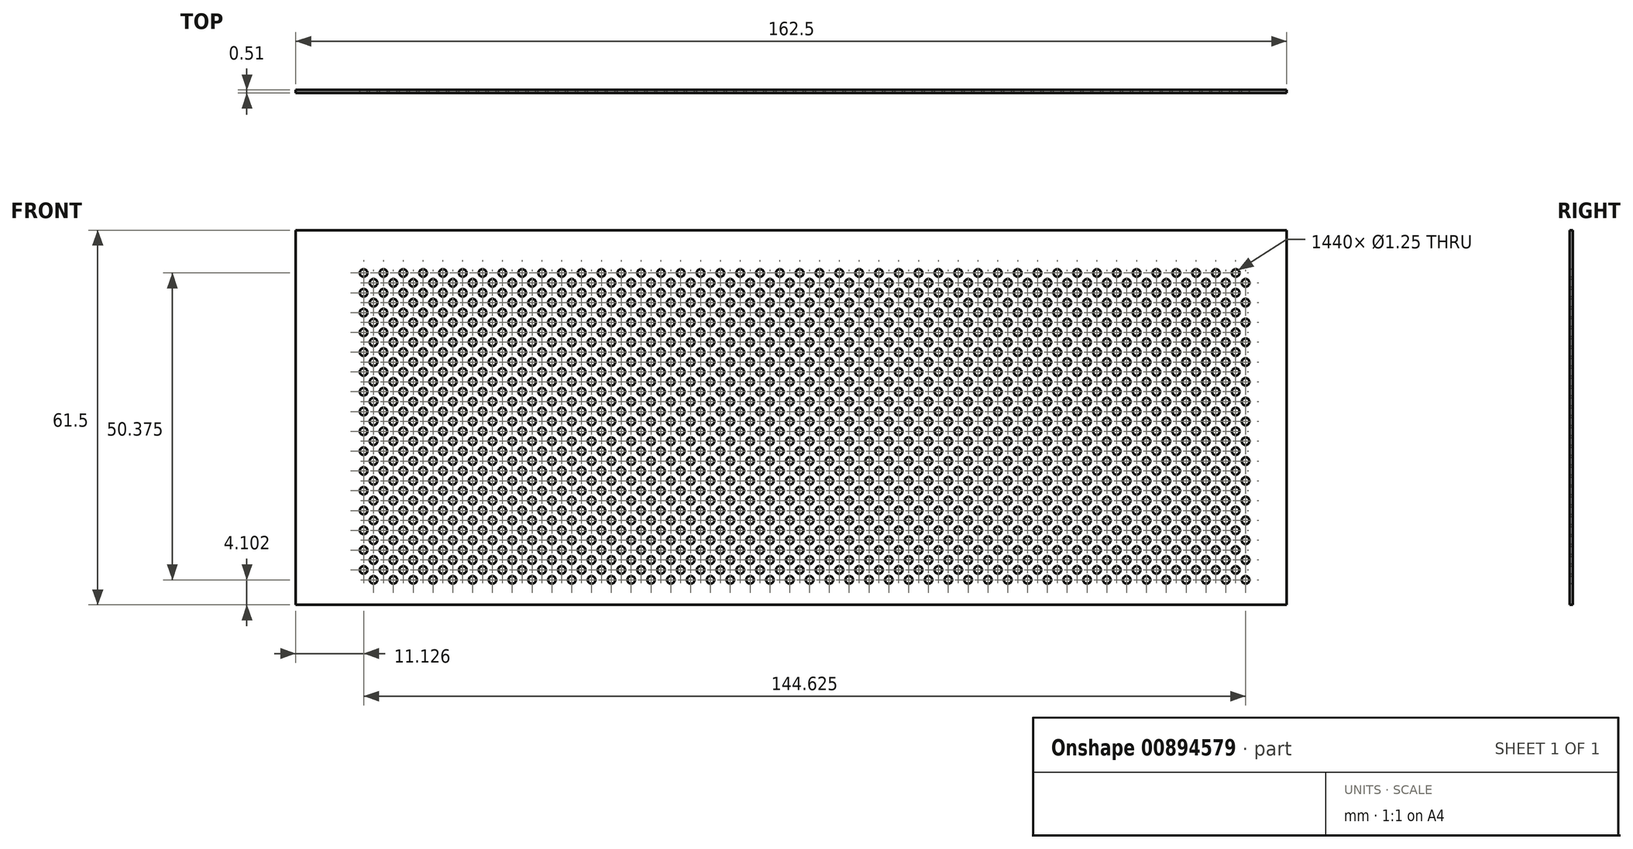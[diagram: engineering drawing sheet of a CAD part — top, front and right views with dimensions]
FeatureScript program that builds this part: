
annotation { "Feature Type Name" : "Feature", "Feature Type Description" : "" }
export const myFeature = defineFeature(function(context is Context, id is Id, definition is map)
    precondition{}
    {
        {
            var Q0;
            Q0=qCreatedBy(makeId("Front.planeOp"),FACE);
            var sketch = newSketch(context, id + "F0", { "sketchPlane" : qUnion([Q0])});
            skLineSegment(sketch, "E0.bottom", {"start": v(-80.2, 17) * mm, "end": v(82.3, 17) * mm});
            skLineSegment(sketch, "E0.top", {"start": v(-80.2, -44.5) * mm, "end": v(82.3, -44.5) * mm});
            skLineSegment(sketch, "E0.left", {"start": v(-80.2, 17) * mm, "end": v(-80.2, -44.5) * mm});
            skLineSegment(sketch, "E0.right", {"start": v(82.3, 17) * mm, "end": v(82.3, -44.5) * mm});
            skCircle(sketch, "E1", {"center": v(-69.07, 9.97) * mm, "radius": 0.62 * mm});
            skCircle(sketch, "E2.0.1.0", {"center": v(-69.07, 6.72) * mm, "radius": 0.62 * mm});
            skCircle(sketch, "E2.0.2.0", {"center": v(-69.07, 3.47) * mm, "radius": 0.62 * mm});
            skCircle(sketch, "E2.1.0.0", {"center": v(-65.82, 9.97) * mm, "radius": 0.62 * mm});
            skCircle(sketch, "E2.1.1.0", {"center": v(-65.82, 6.72) * mm, "radius": 0.62 * mm});
            skCircle(sketch, "E2.1.2.0", {"center": v(-65.82, 3.47) * mm, "radius": 0.62 * mm});
            skCircle(sketch, "E2.2.0.0", {"center": v(-62.57, 9.97) * mm, "radius": 0.62 * mm});
            skCircle(sketch, "E2.2.1.0", {"center": v(-62.57, 6.72) * mm, "radius": 0.62 * mm});
            skCircle(sketch, "E2.2.2.0", {"center": v(-62.57, 3.47) * mm, "radius": 0.62 * mm});
            skCircle(sketch, "E2.3.0.0", {"center": v(-59.32, 9.97) * mm, "radius": 0.62 * mm});
            skCircle(sketch, "E2.3.1.0", {"center": v(-59.32, 6.72) * mm, "radius": 0.62 * mm});
            skCircle(sketch, "E2.3.2.0", {"center": v(-59.32, 3.47) * mm, "radius": 0.62 * mm});
            skCircle(sketch, "E2.4.0.0", {"center": v(-56.07, 9.97) * mm, "radius": 0.62 * mm});
            skCircle(sketch, "E2.4.1.0", {"center": v(-56.07, 6.72) * mm, "radius": 0.62 * mm});
            skCircle(sketch, "E2.4.2.0", {"center": v(-56.07, 3.47) * mm, "radius": 0.62 * mm});
            skCircle(sketch, "E2.5.0.0", {"center": v(-52.82, 9.97) * mm, "radius": 0.62 * mm});
            skCircle(sketch, "E2.5.1.0", {"center": v(-52.82, 6.72) * mm, "radius": 0.62 * mm});
            skCircle(sketch, "E2.5.2.0", {"center": v(-52.82, 3.47) * mm, "radius": 0.62 * mm});
            skCircle(sketch, "E2.6.0.0", {"center": v(-49.57, 9.97) * mm, "radius": 0.62 * mm});
            skCircle(sketch, "E2.6.1.0", {"center": v(-49.57, 6.72) * mm, "radius": 0.62 * mm});
            skCircle(sketch, "E2.6.2.0", {"center": v(-49.57, 3.47) * mm, "radius": 0.62 * mm});
            skCircle(sketch, "E2.7.0.0", {"center": v(-46.32, 9.97) * mm, "radius": 0.62 * mm});
            skCircle(sketch, "E2.7.1.0", {"center": v(-46.32, 6.72) * mm, "radius": 0.62 * mm});
            skCircle(sketch, "E2.7.2.0", {"center": v(-46.32, 3.47) * mm, "radius": 0.62 * mm});
            skCircle(sketch, "E2.8.0.0", {"center": v(-43.07, 9.97) * mm, "radius": 0.62 * mm});
            skCircle(sketch, "E2.8.1.0", {"center": v(-43.07, 6.72) * mm, "radius": 0.62 * mm});
            skCircle(sketch, "E2.8.2.0", {"center": v(-43.07, 3.47) * mm, "radius": 0.62 * mm});
            skCircle(sketch, "E2.9.0.0", {"center": v(-39.82, 9.97) * mm, "radius": 0.62 * mm});
            skCircle(sketch, "E2.9.1.0", {"center": v(-39.82, 6.72) * mm, "radius": 0.62 * mm});
            skCircle(sketch, "E2.9.2.0", {"center": v(-39.82, 3.47) * mm, "radius": 0.62 * mm});
            skCircle(sketch, "E2.10.0.0", {"center": v(-36.57, 9.97) * mm, "radius": 0.62 * mm});
            skCircle(sketch, "E2.10.1.0", {"center": v(-36.57, 6.72) * mm, "radius": 0.62 * mm});
            skCircle(sketch, "E2.10.2.0", {"center": v(-36.57, 3.47) * mm, "radius": 0.62 * mm});
            skCircle(sketch, "E2.11.0.0", {"center": v(-33.32, 9.97) * mm, "radius": 0.62 * mm});
            skCircle(sketch, "E2.11.1.0", {"center": v(-33.32, 6.72) * mm, "radius": 0.62 * mm});
            skCircle(sketch, "E2.11.2.0", {"center": v(-33.32, 3.47) * mm, "radius": 0.62 * mm});
            skCircle(sketch, "E2.12.0.0", {"center": v(-30.07, 9.97) * mm, "radius": 0.62 * mm});
            skCircle(sketch, "E2.12.1.0", {"center": v(-30.07, 6.72) * mm, "radius": 0.62 * mm});
            skCircle(sketch, "E2.12.2.0", {"center": v(-30.07, 3.47) * mm, "radius": 0.62 * mm});
            skCircle(sketch, "E2.13.0.0", {"center": v(-26.82, 9.97) * mm, "radius": 0.62 * mm});
            skCircle(sketch, "E2.13.1.0", {"center": v(-26.82, 6.72) * mm, "radius": 0.62 * mm});
            skCircle(sketch, "E2.13.2.0", {"center": v(-26.82, 3.47) * mm, "radius": 0.62 * mm});
            skCircle(sketch, "E2.14.0.0", {"center": v(-23.57, 9.97) * mm, "radius": 0.62 * mm});
            skCircle(sketch, "E2.14.1.0", {"center": v(-23.57, 6.72) * mm, "radius": 0.62 * mm});
            skCircle(sketch, "E2.14.2.0", {"center": v(-23.57, 3.47) * mm, "radius": 0.62 * mm});
            skCircle(sketch, "E2.15.0.0", {"center": v(-20.32, 9.97) * mm, "radius": 0.62 * mm});
            skCircle(sketch, "E2.15.1.0", {"center": v(-20.32, 6.72) * mm, "radius": 0.62 * mm});
            skCircle(sketch, "E2.15.2.0", {"center": v(-20.32, 3.47) * mm, "radius": 0.62 * mm});
            skCircle(sketch, "E2.16.0.0", {"center": v(-17.07, 9.97) * mm, "radius": 0.62 * mm});
            skCircle(sketch, "E2.16.1.0", {"center": v(-17.07, 6.72) * mm, "radius": 0.62 * mm});
            skCircle(sketch, "E2.16.2.0", {"center": v(-17.07, 3.47) * mm, "radius": 0.62 * mm});
            skCircle(sketch, "E2.17.0.0", {"center": v(-13.82, 9.97) * mm, "radius": 0.62 * mm});
            skCircle(sketch, "E2.17.1.0", {"center": v(-13.82, 6.72) * mm, "radius": 0.62 * mm});
            skCircle(sketch, "E2.17.2.0", {"center": v(-13.82, 3.47) * mm, "radius": 0.62 * mm});
            skCircle(sketch, "E2.18.0.0", {"center": v(-10.57, 9.97) * mm, "radius": 0.62 * mm});
            skCircle(sketch, "E2.18.1.0", {"center": v(-10.57, 6.72) * mm, "radius": 0.62 * mm});
            skCircle(sketch, "E2.18.2.0", {"center": v(-10.57, 3.47) * mm, "radius": 0.62 * mm});
            skCircle(sketch, "E2.19.0.0", {"center": v(-7.32, 9.97) * mm, "radius": 0.62 * mm});
            skCircle(sketch, "E2.19.1.0", {"center": v(-7.32, 6.72) * mm, "radius": 0.62 * mm});
            skCircle(sketch, "E2.19.2.0", {"center": v(-7.32, 3.47) * mm, "radius": 0.62 * mm});
            skLineSegment(sketch, "E2.direction1", {"start": v(-69.07, 9.97) * mm, "end": v(-65.82, 9.97) * mm, "construction": true});
            skLineSegment(sketch, "E2.direction2", {"start": v(-69.07, 9.97) * mm, "end": v(-69.07, 6.72) * mm, "construction": true});
            skCircle(sketch, "E3.0.20.0", {"center": v(-4.07, 9.97) * mm, "radius": 0.62 * mm});
            skCircle(sketch, "E3.0.20.1", {"center": v(-4.07, 6.72) * mm, "radius": 0.62 * mm});
            skCircle(sketch, "E3.0.20.2", {"center": v(-4.07, 3.47) * mm, "radius": 0.62 * mm});
            skCircle(sketch, "E3.0.21.0", {"center": v(-0.82, 9.97) * mm, "radius": 0.62 * mm});
            skCircle(sketch, "E3.0.21.1", {"center": v(-0.82, 6.72) * mm, "radius": 0.62 * mm});
            skCircle(sketch, "E3.0.21.2", {"center": v(-0.82, 3.47) * mm, "radius": 0.62 * mm});
            skCircle(sketch, "E3.0.22.0", {"center": v(2.43, 9.97) * mm, "radius": 0.62 * mm});
            skCircle(sketch, "E3.0.22.1", {"center": v(2.43, 6.72) * mm, "radius": 0.62 * mm});
            skCircle(sketch, "E3.0.22.2", {"center": v(2.43, 3.47) * mm, "radius": 0.62 * mm});
            skCircle(sketch, "E3.0.23.0", {"center": v(5.68, 9.97) * mm, "radius": 0.62 * mm});
            skCircle(sketch, "E3.0.23.1", {"center": v(5.68, 6.72) * mm, "radius": 0.62 * mm});
            skCircle(sketch, "E3.0.23.2", {"center": v(5.68, 3.47) * mm, "radius": 0.62 * mm});
            skCircle(sketch, "E3.0.24.0", {"center": v(8.93, 9.97) * mm, "radius": 0.62 * mm});
            skCircle(sketch, "E3.0.24.1", {"center": v(8.93, 6.72) * mm, "radius": 0.62 * mm});
            skCircle(sketch, "E3.0.24.2", {"center": v(8.93, 3.47) * mm, "radius": 0.62 * mm});
            skCircle(sketch, "E3.0.25.0", {"center": v(12.18, 9.97) * mm, "radius": 0.62 * mm});
            skCircle(sketch, "E3.0.25.1", {"center": v(12.18, 6.72) * mm, "radius": 0.62 * mm});
            skCircle(sketch, "E3.0.25.2", {"center": v(12.18, 3.47) * mm, "radius": 0.62 * mm});
            skCircle(sketch, "E3.0.26.0", {"center": v(15.43, 9.97) * mm, "radius": 0.62 * mm});
            skCircle(sketch, "E3.0.26.1", {"center": v(15.43, 6.72) * mm, "radius": 0.62 * mm});
            skCircle(sketch, "E3.0.26.2", {"center": v(15.43, 3.47) * mm, "radius": 0.62 * mm});
            skCircle(sketch, "E3.0.27.0", {"center": v(18.68, 9.97) * mm, "radius": 0.62 * mm});
            skCircle(sketch, "E3.0.27.1", {"center": v(18.68, 6.72) * mm, "radius": 0.62 * mm});
            skCircle(sketch, "E3.0.27.2", {"center": v(18.68, 3.47) * mm, "radius": 0.62 * mm});
            skCircle(sketch, "E3.0.28.0", {"center": v(21.93, 9.97) * mm, "radius": 0.62 * mm});
            skCircle(sketch, "E3.0.28.1", {"center": v(21.93, 6.72) * mm, "radius": 0.62 * mm});
            skCircle(sketch, "E3.0.28.2", {"center": v(21.93, 3.47) * mm, "radius": 0.62 * mm});
            skCircle(sketch, "E3.0.29.0", {"center": v(25.18, 9.97) * mm, "radius": 0.62 * mm});
            skCircle(sketch, "E3.0.29.1", {"center": v(25.18, 6.72) * mm, "radius": 0.62 * mm});
            skCircle(sketch, "E3.0.29.2", {"center": v(25.18, 3.47) * mm, "radius": 0.62 * mm});
            skCircle(sketch, "E4", {"center": v(-67.45, 8.34) * mm, "radius": 0.62 * mm});
            skLineSegment(sketch, "E5", {"start": v(-65.82, 6.72) * mm, "end": v(-69.07, 9.97) * mm});
            skCircle(sketch, "E6.0.0.3", {"center": v(-69.07, 0.22) * mm, "radius": 0.62 * mm});
            skCircle(sketch, "E6.0.0.4", {"center": v(-69.07, -3.03) * mm, "radius": 0.62 * mm});
            skCircle(sketch, "E6.0.0.5", {"center": v(-69.07, -6.28) * mm, "radius": 0.62 * mm});
            skCircle(sketch, "E6.0.1.3", {"center": v(-65.82, 0.22) * mm, "radius": 0.62 * mm});
            skCircle(sketch, "E6.0.1.4", {"center": v(-65.82, -3.03) * mm, "radius": 0.62 * mm});
            skCircle(sketch, "E6.0.1.5", {"center": v(-65.82, -6.28) * mm, "radius": 0.62 * mm});
            skCircle(sketch, "E6.0.2.3", {"center": v(-62.57, 0.22) * mm, "radius": 0.62 * mm});
            skCircle(sketch, "E6.0.2.4", {"center": v(-62.57, -3.03) * mm, "radius": 0.62 * mm});
            skCircle(sketch, "E6.0.2.5", {"center": v(-62.57, -6.28) * mm, "radius": 0.62 * mm});
            skCircle(sketch, "E6.0.3.3", {"center": v(-59.32, 0.22) * mm, "radius": 0.62 * mm});
            skCircle(sketch, "E6.0.3.4", {"center": v(-59.32, -3.03) * mm, "radius": 0.62 * mm});
            skCircle(sketch, "E6.0.3.5", {"center": v(-59.32, -6.28) * mm, "radius": 0.62 * mm});
            skCircle(sketch, "E6.0.4.3", {"center": v(-56.07, 0.22) * mm, "radius": 0.62 * mm});
            skCircle(sketch, "E6.0.4.4", {"center": v(-56.07, -3.03) * mm, "radius": 0.62 * mm});
            skCircle(sketch, "E6.0.4.5", {"center": v(-56.07, -6.28) * mm, "radius": 0.62 * mm});
            skCircle(sketch, "E6.0.5.3", {"center": v(-52.82, 0.22) * mm, "radius": 0.62 * mm});
            skCircle(sketch, "E6.0.5.4", {"center": v(-52.82, -3.03) * mm, "radius": 0.62 * mm});
            skCircle(sketch, "E6.0.5.5", {"center": v(-52.82, -6.28) * mm, "radius": 0.62 * mm});
            skCircle(sketch, "E6.0.6.3", {"center": v(-49.57, 0.22) * mm, "radius": 0.62 * mm});
            skCircle(sketch, "E6.0.6.4", {"center": v(-49.57, -3.03) * mm, "radius": 0.62 * mm});
            skCircle(sketch, "E6.0.6.5", {"center": v(-49.57, -6.28) * mm, "radius": 0.62 * mm});
            skCircle(sketch, "E6.0.7.3", {"center": v(-46.32, 0.22) * mm, "radius": 0.62 * mm});
            skCircle(sketch, "E6.0.7.4", {"center": v(-46.32, -3.03) * mm, "radius": 0.62 * mm});
            skCircle(sketch, "E6.0.7.5", {"center": v(-46.32, -6.28) * mm, "radius": 0.62 * mm});
            skCircle(sketch, "E6.0.8.3", {"center": v(-43.07, 0.22) * mm, "radius": 0.62 * mm});
            skCircle(sketch, "E6.0.8.4", {"center": v(-43.07, -3.03) * mm, "radius": 0.62 * mm});
            skCircle(sketch, "E6.0.8.5", {"center": v(-43.07, -6.28) * mm, "radius": 0.62 * mm});
            skCircle(sketch, "E6.0.9.3", {"center": v(-39.82, 0.22) * mm, "radius": 0.62 * mm});
            skCircle(sketch, "E6.0.9.4", {"center": v(-39.82, -3.03) * mm, "radius": 0.62 * mm});
            skCircle(sketch, "E6.0.9.5", {"center": v(-39.82, -6.28) * mm, "radius": 0.62 * mm});
            skCircle(sketch, "E6.0.10.3", {"center": v(-36.57, 0.22) * mm, "radius": 0.62 * mm});
            skCircle(sketch, "E6.0.10.4", {"center": v(-36.57, -3.03) * mm, "radius": 0.62 * mm});
            skCircle(sketch, "E6.0.10.5", {"center": v(-36.57, -6.28) * mm, "radius": 0.62 * mm});
            skCircle(sketch, "E6.0.11.3", {"center": v(-33.32, 0.22) * mm, "radius": 0.62 * mm});
            skCircle(sketch, "E6.0.11.4", {"center": v(-33.32, -3.03) * mm, "radius": 0.62 * mm});
            skCircle(sketch, "E6.0.11.5", {"center": v(-33.32, -6.28) * mm, "radius": 0.62 * mm});
            skCircle(sketch, "E6.0.12.3", {"center": v(-30.07, 0.22) * mm, "radius": 0.62 * mm});
            skCircle(sketch, "E6.0.12.4", {"center": v(-30.07, -3.03) * mm, "radius": 0.62 * mm});
            skCircle(sketch, "E6.0.12.5", {"center": v(-30.07, -6.28) * mm, "radius": 0.62 * mm});
            skCircle(sketch, "E6.0.13.3", {"center": v(-26.82, 0.22) * mm, "radius": 0.62 * mm});
            skCircle(sketch, "E6.0.13.4", {"center": v(-26.82, -3.03) * mm, "radius": 0.62 * mm});
            skCircle(sketch, "E6.0.13.5", {"center": v(-26.82, -6.28) * mm, "radius": 0.62 * mm});
            skCircle(sketch, "E6.0.14.3", {"center": v(-23.57, 0.22) * mm, "radius": 0.62 * mm});
            skCircle(sketch, "E6.0.14.4", {"center": v(-23.57, -3.03) * mm, "radius": 0.62 * mm});
            skCircle(sketch, "E6.0.14.5", {"center": v(-23.57, -6.28) * mm, "radius": 0.62 * mm});
            skCircle(sketch, "E6.0.15.3", {"center": v(-20.32, 0.22) * mm, "radius": 0.62 * mm});
            skCircle(sketch, "E6.0.15.4", {"center": v(-20.32, -3.03) * mm, "radius": 0.62 * mm});
            skCircle(sketch, "E6.0.15.5", {"center": v(-20.32, -6.28) * mm, "radius": 0.62 * mm});
            skCircle(sketch, "E6.0.16.3", {"center": v(-17.07, 0.22) * mm, "radius": 0.62 * mm});
            skCircle(sketch, "E6.0.16.4", {"center": v(-17.07, -3.03) * mm, "radius": 0.62 * mm});
            skCircle(sketch, "E6.0.16.5", {"center": v(-17.07, -6.28) * mm, "radius": 0.62 * mm});
            skCircle(sketch, "E6.0.17.3", {"center": v(-13.82, 0.22) * mm, "radius": 0.62 * mm});
            skCircle(sketch, "E6.0.17.4", {"center": v(-13.82, -3.03) * mm, "radius": 0.62 * mm});
            skCircle(sketch, "E6.0.17.5", {"center": v(-13.82, -6.28) * mm, "radius": 0.62 * mm});
            skCircle(sketch, "E6.0.18.3", {"center": v(-10.57, 0.22) * mm, "radius": 0.62 * mm});
            skCircle(sketch, "E6.0.18.4", {"center": v(-10.57, -3.03) * mm, "radius": 0.62 * mm});
            skCircle(sketch, "E6.0.18.5", {"center": v(-10.57, -6.28) * mm, "radius": 0.62 * mm});
            skCircle(sketch, "E6.0.19.3", {"center": v(-7.32, 0.22) * mm, "radius": 0.62 * mm});
            skCircle(sketch, "E6.0.19.4", {"center": v(-7.32, -3.03) * mm, "radius": 0.62 * mm});
            skCircle(sketch, "E6.0.19.5", {"center": v(-7.32, -6.28) * mm, "radius": 0.62 * mm});
            skCircle(sketch, "E6.0.20.3", {"center": v(-4.07, 0.22) * mm, "radius": 0.62 * mm});
            skCircle(sketch, "E6.0.20.4", {"center": v(-4.07, -3.03) * mm, "radius": 0.62 * mm});
            skCircle(sketch, "E6.0.20.5", {"center": v(-4.07, -6.28) * mm, "radius": 0.62 * mm});
            skCircle(sketch, "E6.0.21.3", {"center": v(-0.82, 0.22) * mm, "radius": 0.62 * mm});
            skCircle(sketch, "E6.0.21.4", {"center": v(-0.82, -3.03) * mm, "radius": 0.62 * mm});
            skCircle(sketch, "E6.0.21.5", {"center": v(-0.82, -6.28) * mm, "radius": 0.62 * mm});
            skCircle(sketch, "E6.0.22.3", {"center": v(2.43, 0.22) * mm, "radius": 0.62 * mm});
            skCircle(sketch, "E6.0.22.4", {"center": v(2.43, -3.03) * mm, "radius": 0.62 * mm});
            skCircle(sketch, "E6.0.22.5", {"center": v(2.43, -6.28) * mm, "radius": 0.62 * mm});
            skCircle(sketch, "E6.0.23.3", {"center": v(5.68, 0.22) * mm, "radius": 0.62 * mm});
            skCircle(sketch, "E6.0.23.4", {"center": v(5.68, -3.03) * mm, "radius": 0.62 * mm});
            skCircle(sketch, "E6.0.23.5", {"center": v(5.68, -6.28) * mm, "radius": 0.62 * mm});
            skCircle(sketch, "E6.0.24.3", {"center": v(8.93, 0.22) * mm, "radius": 0.62 * mm});
            skCircle(sketch, "E6.0.24.4", {"center": v(8.93, -3.03) * mm, "radius": 0.62 * mm});
            skCircle(sketch, "E6.0.24.5", {"center": v(8.93, -6.28) * mm, "radius": 0.62 * mm});
            skCircle(sketch, "E6.0.25.3", {"center": v(12.18, 0.22) * mm, "radius": 0.62 * mm});
            skCircle(sketch, "E6.0.25.4", {"center": v(12.18, -3.03) * mm, "radius": 0.62 * mm});
            skCircle(sketch, "E6.0.25.5", {"center": v(12.18, -6.28) * mm, "radius": 0.62 * mm});
            skCircle(sketch, "E6.0.26.3", {"center": v(15.43, 0.22) * mm, "radius": 0.62 * mm});
            skCircle(sketch, "E6.0.26.4", {"center": v(15.43, -3.03) * mm, "radius": 0.62 * mm});
            skCircle(sketch, "E6.0.26.5", {"center": v(15.43, -6.28) * mm, "radius": 0.62 * mm});
            skCircle(sketch, "E6.0.27.3", {"center": v(18.68, 0.22) * mm, "radius": 0.62 * mm});
            skCircle(sketch, "E6.0.27.4", {"center": v(18.68, -3.03) * mm, "radius": 0.62 * mm});
            skCircle(sketch, "E6.0.27.5", {"center": v(18.68, -6.28) * mm, "radius": 0.62 * mm});
            skCircle(sketch, "E6.0.28.3", {"center": v(21.93, 0.22) * mm, "radius": 0.62 * mm});
            skCircle(sketch, "E6.0.28.4", {"center": v(21.93, -3.03) * mm, "radius": 0.62 * mm});
            skCircle(sketch, "E6.0.28.5", {"center": v(21.93, -6.28) * mm, "radius": 0.62 * mm});
            skCircle(sketch, "E6.0.29.3", {"center": v(25.18, 0.22) * mm, "radius": 0.62 * mm});
            skCircle(sketch, "E6.0.29.4", {"center": v(25.18, -3.03) * mm, "radius": 0.62 * mm});
            skCircle(sketch, "E6.0.29.5", {"center": v(25.18, -6.28) * mm, "radius": 0.62 * mm});
            skCircle(sketch, "E7.0.1.0", {"center": v(-67.45, 5.1) * mm, "radius": 0.62 * mm});
            skCircle(sketch, "E7.0.2.0", {"center": v(-67.45, 1.84) * mm, "radius": 0.62 * mm});
            skCircle(sketch, "E7.0.3.0", {"center": v(-67.45, -1.4) * mm, "radius": 0.62 * mm});
            skCircle(sketch, "E7.0.4.0", {"center": v(-67.45, -4.66) * mm, "radius": 0.62 * mm});
            skCircle(sketch, "E7.0.5.0", {"center": v(-67.45, -7.9) * mm, "radius": 0.62 * mm});
            skCircle(sketch, "E7.1.0.0", {"center": v(-64.2, 8.34) * mm, "radius": 0.62 * mm});
            skCircle(sketch, "E7.1.1.0", {"center": v(-64.2, 5.1) * mm, "radius": 0.62 * mm});
            skCircle(sketch, "E7.1.2.0", {"center": v(-64.2, 1.84) * mm, "radius": 0.62 * mm});
            skCircle(sketch, "E7.1.3.0", {"center": v(-64.2, -1.4) * mm, "radius": 0.62 * mm});
            skCircle(sketch, "E7.1.4.0", {"center": v(-64.2, -4.66) * mm, "radius": 0.62 * mm});
            skCircle(sketch, "E7.1.5.0", {"center": v(-64.2, -7.9) * mm, "radius": 0.62 * mm});
            skCircle(sketch, "E7.2.0.0", {"center": v(-60.95, 8.34) * mm, "radius": 0.62 * mm});
            skCircle(sketch, "E7.2.1.0", {"center": v(-60.95, 5.1) * mm, "radius": 0.62 * mm});
            skCircle(sketch, "E7.2.2.0", {"center": v(-60.95, 1.84) * mm, "radius": 0.62 * mm});
            skCircle(sketch, "E7.2.3.0", {"center": v(-60.95, -1.4) * mm, "radius": 0.62 * mm});
            skCircle(sketch, "E7.2.4.0", {"center": v(-60.95, -4.66) * mm, "radius": 0.62 * mm});
            skCircle(sketch, "E7.2.5.0", {"center": v(-60.95, -7.9) * mm, "radius": 0.62 * mm});
            skCircle(sketch, "E7.3.0.0", {"center": v(-57.7, 8.34) * mm, "radius": 0.62 * mm});
            skCircle(sketch, "E7.3.1.0", {"center": v(-57.7, 5.1) * mm, "radius": 0.62 * mm});
            skCircle(sketch, "E7.3.2.0", {"center": v(-57.7, 1.84) * mm, "radius": 0.62 * mm});
            skCircle(sketch, "E7.3.3.0", {"center": v(-57.7, -1.4) * mm, "radius": 0.62 * mm});
            skCircle(sketch, "E7.3.4.0", {"center": v(-57.7, -4.66) * mm, "radius": 0.62 * mm});
            skCircle(sketch, "E7.3.5.0", {"center": v(-57.7, -7.9) * mm, "radius": 0.62 * mm});
            skCircle(sketch, "E7.4.0.0", {"center": v(-54.45, 8.34) * mm, "radius": 0.62 * mm});
            skCircle(sketch, "E7.4.1.0", {"center": v(-54.45, 5.1) * mm, "radius": 0.62 * mm});
            skCircle(sketch, "E7.4.2.0", {"center": v(-54.45, 1.84) * mm, "radius": 0.62 * mm});
            skCircle(sketch, "E7.4.3.0", {"center": v(-54.45, -1.4) * mm, "radius": 0.62 * mm});
            skCircle(sketch, "E7.4.4.0", {"center": v(-54.45, -4.66) * mm, "radius": 0.62 * mm});
            skCircle(sketch, "E7.4.5.0", {"center": v(-54.45, -7.9) * mm, "radius": 0.62 * mm});
            skCircle(sketch, "E7.5.0.0", {"center": v(-51.2, 8.34) * mm, "radius": 0.62 * mm});
            skCircle(sketch, "E7.5.1.0", {"center": v(-51.2, 5.1) * mm, "radius": 0.62 * mm});
            skCircle(sketch, "E7.5.2.0", {"center": v(-51.2, 1.84) * mm, "radius": 0.62 * mm});
            skCircle(sketch, "E7.5.3.0", {"center": v(-51.2, -1.4) * mm, "radius": 0.62 * mm});
            skCircle(sketch, "E7.5.4.0", {"center": v(-51.2, -4.66) * mm, "radius": 0.62 * mm});
            skCircle(sketch, "E7.5.5.0", {"center": v(-51.2, -7.9) * mm, "radius": 0.62 * mm});
            skCircle(sketch, "E7.6.0.0", {"center": v(-47.95, 8.34) * mm, "radius": 0.62 * mm});
            skCircle(sketch, "E7.6.1.0", {"center": v(-47.95, 5.1) * mm, "radius": 0.62 * mm});
            skCircle(sketch, "E7.6.2.0", {"center": v(-47.95, 1.84) * mm, "radius": 0.62 * mm});
            skCircle(sketch, "E7.6.3.0", {"center": v(-47.95, -1.4) * mm, "radius": 0.62 * mm});
            skCircle(sketch, "E7.6.4.0", {"center": v(-47.95, -4.66) * mm, "radius": 0.62 * mm});
            skCircle(sketch, "E7.6.5.0", {"center": v(-47.95, -7.9) * mm, "radius": 0.62 * mm});
            skCircle(sketch, "E7.7.0.0", {"center": v(-44.7, 8.34) * mm, "radius": 0.62 * mm});
            skCircle(sketch, "E7.7.1.0", {"center": v(-44.7, 5.1) * mm, "radius": 0.62 * mm});
            skCircle(sketch, "E7.7.2.0", {"center": v(-44.7, 1.84) * mm, "radius": 0.62 * mm});
            skCircle(sketch, "E7.7.3.0", {"center": v(-44.7, -1.4) * mm, "radius": 0.62 * mm});
            skCircle(sketch, "E7.7.4.0", {"center": v(-44.7, -4.66) * mm, "radius": 0.62 * mm});
            skCircle(sketch, "E7.7.5.0", {"center": v(-44.7, -7.9) * mm, "radius": 0.62 * mm});
            skCircle(sketch, "E7.8.0.0", {"center": v(-41.45, 8.34) * mm, "radius": 0.62 * mm});
            skCircle(sketch, "E7.8.1.0", {"center": v(-41.45, 5.1) * mm, "radius": 0.62 * mm});
            skCircle(sketch, "E7.8.2.0", {"center": v(-41.45, 1.84) * mm, "radius": 0.62 * mm});
            skCircle(sketch, "E7.8.3.0", {"center": v(-41.45, -1.4) * mm, "radius": 0.62 * mm});
            skCircle(sketch, "E7.8.4.0", {"center": v(-41.45, -4.66) * mm, "radius": 0.62 * mm});
            skCircle(sketch, "E7.8.5.0", {"center": v(-41.45, -7.9) * mm, "radius": 0.62 * mm});
            skCircle(sketch, "E7.9.0.0", {"center": v(-38.2, 8.34) * mm, "radius": 0.62 * mm});
            skCircle(sketch, "E7.9.1.0", {"center": v(-38.2, 5.1) * mm, "radius": 0.62 * mm});
            skCircle(sketch, "E7.9.2.0", {"center": v(-38.2, 1.84) * mm, "radius": 0.62 * mm});
            skCircle(sketch, "E7.9.3.0", {"center": v(-38.2, -1.4) * mm, "radius": 0.62 * mm});
            skCircle(sketch, "E7.9.4.0", {"center": v(-38.2, -4.66) * mm, "radius": 0.62 * mm});
            skCircle(sketch, "E7.9.5.0", {"center": v(-38.2, -7.9) * mm, "radius": 0.62 * mm});
            skCircle(sketch, "E7.10.0.0", {"center": v(-34.95, 8.34) * mm, "radius": 0.62 * mm});
            skCircle(sketch, "E7.10.1.0", {"center": v(-34.95, 5.1) * mm, "radius": 0.62 * mm});
            skCircle(sketch, "E7.10.2.0", {"center": v(-34.95, 1.84) * mm, "radius": 0.62 * mm});
            skCircle(sketch, "E7.10.3.0", {"center": v(-34.95, -1.4) * mm, "radius": 0.62 * mm});
            skCircle(sketch, "E7.10.4.0", {"center": v(-34.95, -4.66) * mm, "radius": 0.62 * mm});
            skCircle(sketch, "E7.10.5.0", {"center": v(-34.95, -7.9) * mm, "radius": 0.62 * mm});
            skCircle(sketch, "E7.11.0.0", {"center": v(-31.7, 8.34) * mm, "radius": 0.62 * mm});
            skCircle(sketch, "E7.11.1.0", {"center": v(-31.7, 5.1) * mm, "radius": 0.62 * mm});
            skCircle(sketch, "E7.11.2.0", {"center": v(-31.7, 1.84) * mm, "radius": 0.62 * mm});
            skCircle(sketch, "E7.11.3.0", {"center": v(-31.7, -1.4) * mm, "radius": 0.62 * mm});
            skCircle(sketch, "E7.11.4.0", {"center": v(-31.7, -4.66) * mm, "radius": 0.62 * mm});
            skCircle(sketch, "E7.11.5.0", {"center": v(-31.7, -7.9) * mm, "radius": 0.62 * mm});
            skCircle(sketch, "E7.12.0.0", {"center": v(-28.45, 8.34) * mm, "radius": 0.62 * mm});
            skCircle(sketch, "E7.12.1.0", {"center": v(-28.45, 5.1) * mm, "radius": 0.62 * mm});
            skCircle(sketch, "E7.12.2.0", {"center": v(-28.45, 1.84) * mm, "radius": 0.62 * mm});
            skCircle(sketch, "E7.12.3.0", {"center": v(-28.45, -1.4) * mm, "radius": 0.62 * mm});
            skCircle(sketch, "E7.12.4.0", {"center": v(-28.45, -4.66) * mm, "radius": 0.62 * mm});
            skCircle(sketch, "E7.12.5.0", {"center": v(-28.45, -7.9) * mm, "radius": 0.62 * mm});
            skCircle(sketch, "E7.13.0.0", {"center": v(-25.2, 8.34) * mm, "radius": 0.62 * mm});
            skCircle(sketch, "E7.13.1.0", {"center": v(-25.2, 5.1) * mm, "radius": 0.62 * mm});
            skCircle(sketch, "E7.13.2.0", {"center": v(-25.2, 1.84) * mm, "radius": 0.62 * mm});
            skCircle(sketch, "E7.13.3.0", {"center": v(-25.2, -1.4) * mm, "radius": 0.62 * mm});
            skCircle(sketch, "E7.13.4.0", {"center": v(-25.2, -4.66) * mm, "radius": 0.62 * mm});
            skCircle(sketch, "E7.13.5.0", {"center": v(-25.2, -7.9) * mm, "radius": 0.62 * mm});
            skCircle(sketch, "E7.14.0.0", {"center": v(-21.95, 8.34) * mm, "radius": 0.62 * mm});
            skCircle(sketch, "E7.14.1.0", {"center": v(-21.95, 5.1) * mm, "radius": 0.62 * mm});
            skCircle(sketch, "E7.14.2.0", {"center": v(-21.95, 1.84) * mm, "radius": 0.62 * mm});
            skCircle(sketch, "E7.14.3.0", {"center": v(-21.95, -1.4) * mm, "radius": 0.62 * mm});
            skCircle(sketch, "E7.14.4.0", {"center": v(-21.95, -4.66) * mm, "radius": 0.62 * mm});
            skCircle(sketch, "E7.14.5.0", {"center": v(-21.95, -7.9) * mm, "radius": 0.62 * mm});
            skCircle(sketch, "E7.15.0.0", {"center": v(-18.7, 8.34) * mm, "radius": 0.62 * mm});
            skCircle(sketch, "E7.15.1.0", {"center": v(-18.7, 5.1) * mm, "radius": 0.62 * mm});
            skCircle(sketch, "E7.15.2.0", {"center": v(-18.7, 1.84) * mm, "radius": 0.62 * mm});
            skCircle(sketch, "E7.15.3.0", {"center": v(-18.7, -1.4) * mm, "radius": 0.62 * mm});
            skCircle(sketch, "E7.15.4.0", {"center": v(-18.7, -4.66) * mm, "radius": 0.62 * mm});
            skCircle(sketch, "E7.15.5.0", {"center": v(-18.7, -7.9) * mm, "radius": 0.62 * mm});
            skCircle(sketch, "E7.16.0.0", {"center": v(-15.45, 8.34) * mm, "radius": 0.62 * mm});
            skCircle(sketch, "E7.16.1.0", {"center": v(-15.45, 5.1) * mm, "radius": 0.62 * mm});
            skCircle(sketch, "E7.16.2.0", {"center": v(-15.45, 1.84) * mm, "radius": 0.62 * mm});
            skCircle(sketch, "E7.16.3.0", {"center": v(-15.45, -1.4) * mm, "radius": 0.62 * mm});
            skCircle(sketch, "E7.16.4.0", {"center": v(-15.45, -4.66) * mm, "radius": 0.62 * mm});
            skCircle(sketch, "E7.16.5.0", {"center": v(-15.45, -7.9) * mm, "radius": 0.62 * mm});
            skCircle(sketch, "E7.17.0.0", {"center": v(-12.2, 8.34) * mm, "radius": 0.62 * mm});
            skCircle(sketch, "E7.17.1.0", {"center": v(-12.2, 5.1) * mm, "radius": 0.62 * mm});
            skCircle(sketch, "E7.17.2.0", {"center": v(-12.2, 1.84) * mm, "radius": 0.62 * mm});
            skCircle(sketch, "E7.17.3.0", {"center": v(-12.2, -1.4) * mm, "radius": 0.62 * mm});
            skCircle(sketch, "E7.17.4.0", {"center": v(-12.2, -4.66) * mm, "radius": 0.62 * mm});
            skCircle(sketch, "E7.17.5.0", {"center": v(-12.2, -7.9) * mm, "radius": 0.62 * mm});
            skCircle(sketch, "E7.18.0.0", {"center": v(-8.95, 8.34) * mm, "radius": 0.62 * mm});
            skCircle(sketch, "E7.18.1.0", {"center": v(-8.95, 5.1) * mm, "radius": 0.62 * mm});
            skCircle(sketch, "E7.18.2.0", {"center": v(-8.95, 1.84) * mm, "radius": 0.62 * mm});
            skCircle(sketch, "E7.18.3.0", {"center": v(-8.95, -1.4) * mm, "radius": 0.62 * mm});
            skCircle(sketch, "E7.18.4.0", {"center": v(-8.95, -4.66) * mm, "radius": 0.62 * mm});
            skCircle(sketch, "E7.18.5.0", {"center": v(-8.95, -7.9) * mm, "radius": 0.62 * mm});
            skCircle(sketch, "E7.19.0.0", {"center": v(-5.7, 8.34) * mm, "radius": 0.62 * mm});
            skCircle(sketch, "E7.19.1.0", {"center": v(-5.7, 5.1) * mm, "radius": 0.62 * mm});
            skCircle(sketch, "E7.19.2.0", {"center": v(-5.7, 1.84) * mm, "radius": 0.62 * mm});
            skCircle(sketch, "E7.19.3.0", {"center": v(-5.7, -1.4) * mm, "radius": 0.62 * mm});
            skCircle(sketch, "E7.19.4.0", {"center": v(-5.7, -4.66) * mm, "radius": 0.62 * mm});
            skCircle(sketch, "E7.19.5.0", {"center": v(-5.7, -7.9) * mm, "radius": 0.62 * mm});
            skCircle(sketch, "E7.20.0.0", {"center": v(-2.45, 8.34) * mm, "radius": 0.62 * mm});
            skCircle(sketch, "E7.20.1.0", {"center": v(-2.45, 5.1) * mm, "radius": 0.62 * mm});
            skCircle(sketch, "E7.20.2.0", {"center": v(-2.45, 1.84) * mm, "radius": 0.62 * mm});
            skCircle(sketch, "E7.20.3.0", {"center": v(-2.45, -1.4) * mm, "radius": 0.62 * mm});
            skCircle(sketch, "E7.20.4.0", {"center": v(-2.45, -4.66) * mm, "radius": 0.62 * mm});
            skCircle(sketch, "E7.20.5.0", {"center": v(-2.45, -7.9) * mm, "radius": 0.62 * mm});
            skCircle(sketch, "E7.21.0.0", {"center": v(0.8, 8.34) * mm, "radius": 0.62 * mm});
            skCircle(sketch, "E7.21.1.0", {"center": v(0.8, 5.1) * mm, "radius": 0.62 * mm});
            skCircle(sketch, "E7.21.2.0", {"center": v(0.8, 1.84) * mm, "radius": 0.62 * mm});
            skCircle(sketch, "E7.21.3.0", {"center": v(0.8, -1.4) * mm, "radius": 0.62 * mm});
            skCircle(sketch, "E7.21.4.0", {"center": v(0.8, -4.66) * mm, "radius": 0.62 * mm});
            skCircle(sketch, "E7.21.5.0", {"center": v(0.8, -7.9) * mm, "radius": 0.62 * mm});
            skCircle(sketch, "E7.22.0.0", {"center": v(4.05, 8.34) * mm, "radius": 0.62 * mm});
            skCircle(sketch, "E7.22.1.0", {"center": v(4.05, 5.1) * mm, "radius": 0.62 * mm});
            skCircle(sketch, "E7.22.2.0", {"center": v(4.05, 1.84) * mm, "radius": 0.62 * mm});
            skCircle(sketch, "E7.22.3.0", {"center": v(4.05, -1.4) * mm, "radius": 0.62 * mm});
            skCircle(sketch, "E7.22.4.0", {"center": v(4.05, -4.66) * mm, "radius": 0.62 * mm});
            skCircle(sketch, "E7.22.5.0", {"center": v(4.05, -7.9) * mm, "radius": 0.62 * mm});
            skCircle(sketch, "E7.23.0.0", {"center": v(7.3, 8.34) * mm, "radius": 0.62 * mm});
            skCircle(sketch, "E7.23.1.0", {"center": v(7.3, 5.1) * mm, "radius": 0.62 * mm});
            skCircle(sketch, "E7.23.2.0", {"center": v(7.3, 1.84) * mm, "radius": 0.62 * mm});
            skCircle(sketch, "E7.23.3.0", {"center": v(7.3, -1.4) * mm, "radius": 0.62 * mm});
            skCircle(sketch, "E7.23.4.0", {"center": v(7.3, -4.66) * mm, "radius": 0.62 * mm});
            skCircle(sketch, "E7.23.5.0", {"center": v(7.3, -7.9) * mm, "radius": 0.62 * mm});
            skCircle(sketch, "E7.24.0.0", {"center": v(10.55, 8.34) * mm, "radius": 0.62 * mm});
            skCircle(sketch, "E7.24.1.0", {"center": v(10.55, 5.1) * mm, "radius": 0.62 * mm});
            skCircle(sketch, "E7.24.2.0", {"center": v(10.55, 1.84) * mm, "radius": 0.62 * mm});
            skCircle(sketch, "E7.24.3.0", {"center": v(10.55, -1.4) * mm, "radius": 0.62 * mm});
            skCircle(sketch, "E7.24.4.0", {"center": v(10.55, -4.66) * mm, "radius": 0.62 * mm});
            skCircle(sketch, "E7.24.5.0", {"center": v(10.55, -7.9) * mm, "radius": 0.62 * mm});
            skCircle(sketch, "E7.25.0.0", {"center": v(13.8, 8.34) * mm, "radius": 0.62 * mm});
            skCircle(sketch, "E7.25.1.0", {"center": v(13.8, 5.1) * mm, "radius": 0.62 * mm});
            skCircle(sketch, "E7.25.2.0", {"center": v(13.8, 1.84) * mm, "radius": 0.62 * mm});
            skCircle(sketch, "E7.25.3.0", {"center": v(13.8, -1.4) * mm, "radius": 0.62 * mm});
            skCircle(sketch, "E7.25.4.0", {"center": v(13.8, -4.66) * mm, "radius": 0.62 * mm});
            skCircle(sketch, "E7.25.5.0", {"center": v(13.8, -7.9) * mm, "radius": 0.62 * mm});
            skCircle(sketch, "E7.26.0.0", {"center": v(17.05, 8.34) * mm, "radius": 0.62 * mm});
            skCircle(sketch, "E7.26.1.0", {"center": v(17.05, 5.1) * mm, "radius": 0.62 * mm});
            skCircle(sketch, "E7.26.2.0", {"center": v(17.05, 1.84) * mm, "radius": 0.62 * mm});
            skCircle(sketch, "E7.26.3.0", {"center": v(17.05, -1.4) * mm, "radius": 0.62 * mm});
            skCircle(sketch, "E7.26.4.0", {"center": v(17.05, -4.66) * mm, "radius": 0.62 * mm});
            skCircle(sketch, "E7.26.5.0", {"center": v(17.05, -7.9) * mm, "radius": 0.62 * mm});
            skCircle(sketch, "E7.27.0.0", {"center": v(20.3, 8.34) * mm, "radius": 0.62 * mm});
            skCircle(sketch, "E7.27.1.0", {"center": v(20.3, 5.1) * mm, "radius": 0.62 * mm});
            skCircle(sketch, "E7.27.2.0", {"center": v(20.3, 1.84) * mm, "radius": 0.62 * mm});
            skCircle(sketch, "E7.27.3.0", {"center": v(20.3, -1.4) * mm, "radius": 0.62 * mm});
            skCircle(sketch, "E7.27.4.0", {"center": v(20.3, -4.66) * mm, "radius": 0.62 * mm});
            skCircle(sketch, "E7.27.5.0", {"center": v(20.3, -7.9) * mm, "radius": 0.62 * mm});
            skCircle(sketch, "E7.28.0.0", {"center": v(23.55, 8.34) * mm, "radius": 0.62 * mm});
            skCircle(sketch, "E7.28.1.0", {"center": v(23.55, 5.1) * mm, "radius": 0.62 * mm});
            skCircle(sketch, "E7.28.2.0", {"center": v(23.55, 1.84) * mm, "radius": 0.62 * mm});
            skCircle(sketch, "E7.28.3.0", {"center": v(23.55, -1.4) * mm, "radius": 0.62 * mm});
            skCircle(sketch, "E7.28.4.0", {"center": v(23.55, -4.66) * mm, "radius": 0.62 * mm});
            skCircle(sketch, "E7.28.5.0", {"center": v(23.55, -7.9) * mm, "radius": 0.62 * mm});
            skCircle(sketch, "E7.29.0.0", {"center": v(26.8, 8.34) * mm, "radius": 0.62 * mm});
            skCircle(sketch, "E7.29.1.0", {"center": v(26.8, 5.1) * mm, "radius": 0.62 * mm});
            skCircle(sketch, "E7.29.2.0", {"center": v(26.8, 1.84) * mm, "radius": 0.62 * mm});
            skCircle(sketch, "E7.29.3.0", {"center": v(26.8, -1.4) * mm, "radius": 0.62 * mm});
            skCircle(sketch, "E7.29.4.0", {"center": v(26.8, -4.66) * mm, "radius": 0.62 * mm});
            skCircle(sketch, "E7.29.5.0", {"center": v(26.8, -7.9) * mm, "radius": 0.62 * mm});
            skLineSegment(sketch, "E7.direction1", {"start": v(-67.45, 8.34) * mm, "end": v(-64.2, 8.34) * mm, "construction": true});
            skLineSegment(sketch, "E7.direction2", {"start": v(-67.45, 8.34) * mm, "end": v(-67.45, 5.1) * mm, "construction": true});
            skCircle(sketch, "E8.0.30.0", {"center": v(28.43, 9.97) * mm, "radius": 0.62 * mm});
            skCircle(sketch, "E8.0.30.1", {"center": v(28.43, 6.72) * mm, "radius": 0.62 * mm});
            skCircle(sketch, "E8.0.30.2", {"center": v(28.43, 3.47) * mm, "radius": 0.62 * mm});
            skCircle(sketch, "E8.0.30.3", {"center": v(28.43, 0.22) * mm, "radius": 0.62 * mm});
            skCircle(sketch, "E8.0.30.4", {"center": v(28.43, -3.03) * mm, "radius": 0.62 * mm});
            skCircle(sketch, "E8.0.30.5", {"center": v(28.43, -6.28) * mm, "radius": 0.62 * mm});
            skCircle(sketch, "E8.0.31.0", {"center": v(31.68, 9.97) * mm, "radius": 0.62 * mm});
            skCircle(sketch, "E8.0.31.1", {"center": v(31.68, 6.72) * mm, "radius": 0.62 * mm});
            skCircle(sketch, "E8.0.31.2", {"center": v(31.68, 3.47) * mm, "radius": 0.62 * mm});
            skCircle(sketch, "E8.0.31.3", {"center": v(31.68, 0.22) * mm, "radius": 0.62 * mm});
            skCircle(sketch, "E8.0.31.4", {"center": v(31.68, -3.03) * mm, "radius": 0.62 * mm});
            skCircle(sketch, "E8.0.31.5", {"center": v(31.68, -6.28) * mm, "radius": 0.62 * mm});
            skCircle(sketch, "E8.0.32.0", {"center": v(34.93, 9.97) * mm, "radius": 0.62 * mm});
            skCircle(sketch, "E8.0.32.1", {"center": v(34.93, 6.72) * mm, "radius": 0.62 * mm});
            skCircle(sketch, "E8.0.32.2", {"center": v(34.93, 3.47) * mm, "radius": 0.62 * mm});
            skCircle(sketch, "E8.0.32.3", {"center": v(34.93, 0.22) * mm, "radius": 0.62 * mm});
            skCircle(sketch, "E8.0.32.4", {"center": v(34.93, -3.03) * mm, "radius": 0.62 * mm});
            skCircle(sketch, "E8.0.32.5", {"center": v(34.93, -6.28) * mm, "radius": 0.62 * mm});
            skCircle(sketch, "E8.0.33.0", {"center": v(38.18, 9.97) * mm, "radius": 0.62 * mm});
            skCircle(sketch, "E8.0.33.1", {"center": v(38.18, 6.72) * mm, "radius": 0.62 * mm});
            skCircle(sketch, "E8.0.33.2", {"center": v(38.18, 3.47) * mm, "radius": 0.62 * mm});
            skCircle(sketch, "E8.0.33.3", {"center": v(38.18, 0.22) * mm, "radius": 0.62 * mm});
            skCircle(sketch, "E8.0.33.4", {"center": v(38.18, -3.03) * mm, "radius": 0.62 * mm});
            skCircle(sketch, "E8.0.33.5", {"center": v(38.18, -6.28) * mm, "radius": 0.62 * mm});
            skCircle(sketch, "E8.0.34.0", {"center": v(41.43, 9.97) * mm, "radius": 0.62 * mm});
            skCircle(sketch, "E8.0.34.1", {"center": v(41.43, 6.72) * mm, "radius": 0.62 * mm});
            skCircle(sketch, "E8.0.34.2", {"center": v(41.43, 3.47) * mm, "radius": 0.62 * mm});
            skCircle(sketch, "E8.0.34.3", {"center": v(41.43, 0.22) * mm, "radius": 0.62 * mm});
            skCircle(sketch, "E8.0.34.4", {"center": v(41.43, -3.03) * mm, "radius": 0.62 * mm});
            skCircle(sketch, "E8.0.34.5", {"center": v(41.43, -6.28) * mm, "radius": 0.62 * mm});
            skCircle(sketch, "E8.0.35.0", {"center": v(44.68, 9.97) * mm, "radius": 0.62 * mm});
            skCircle(sketch, "E8.0.35.1", {"center": v(44.68, 6.72) * mm, "radius": 0.62 * mm});
            skCircle(sketch, "E8.0.35.2", {"center": v(44.68, 3.47) * mm, "radius": 0.62 * mm});
            skCircle(sketch, "E8.0.35.3", {"center": v(44.68, 0.22) * mm, "radius": 0.62 * mm});
            skCircle(sketch, "E8.0.35.4", {"center": v(44.68, -3.03) * mm, "radius": 0.62 * mm});
            skCircle(sketch, "E8.0.35.5", {"center": v(44.68, -6.28) * mm, "radius": 0.62 * mm});
            skCircle(sketch, "E8.0.36.0", {"center": v(47.93, 9.97) * mm, "radius": 0.62 * mm});
            skCircle(sketch, "E8.0.36.1", {"center": v(47.93, 6.72) * mm, "radius": 0.62 * mm});
            skCircle(sketch, "E8.0.36.2", {"center": v(47.93, 3.47) * mm, "radius": 0.62 * mm});
            skCircle(sketch, "E8.0.36.3", {"center": v(47.93, 0.22) * mm, "radius": 0.62 * mm});
            skCircle(sketch, "E8.0.36.4", {"center": v(47.93, -3.03) * mm, "radius": 0.62 * mm});
            skCircle(sketch, "E8.0.36.5", {"center": v(47.93, -6.28) * mm, "radius": 0.62 * mm});
            skCircle(sketch, "E8.0.37.0", {"center": v(51.18, 9.97) * mm, "radius": 0.62 * mm});
            skCircle(sketch, "E8.0.37.1", {"center": v(51.18, 6.72) * mm, "radius": 0.62 * mm});
            skCircle(sketch, "E8.0.37.2", {"center": v(51.18, 3.47) * mm, "radius": 0.62 * mm});
            skCircle(sketch, "E8.0.37.3", {"center": v(51.18, 0.22) * mm, "radius": 0.62 * mm});
            skCircle(sketch, "E8.0.37.4", {"center": v(51.18, -3.03) * mm, "radius": 0.62 * mm});
            skCircle(sketch, "E8.0.37.5", {"center": v(51.18, -6.28) * mm, "radius": 0.62 * mm});
            skCircle(sketch, "E8.0.38.0", {"center": v(54.43, 9.97) * mm, "radius": 0.62 * mm});
            skCircle(sketch, "E8.0.38.1", {"center": v(54.43, 6.72) * mm, "radius": 0.62 * mm});
            skCircle(sketch, "E8.0.38.2", {"center": v(54.43, 3.47) * mm, "radius": 0.62 * mm});
            skCircle(sketch, "E8.0.38.3", {"center": v(54.43, 0.22) * mm, "radius": 0.62 * mm});
            skCircle(sketch, "E8.0.38.4", {"center": v(54.43, -3.03) * mm, "radius": 0.62 * mm});
            skCircle(sketch, "E8.0.38.5", {"center": v(54.43, -6.28) * mm, "radius": 0.62 * mm});
            skCircle(sketch, "E8.0.39.0", {"center": v(57.68, 9.97) * mm, "radius": 0.62 * mm});
            skCircle(sketch, "E8.0.39.1", {"center": v(57.68, 6.72) * mm, "radius": 0.62 * mm});
            skCircle(sketch, "E8.0.39.2", {"center": v(57.68, 3.47) * mm, "radius": 0.62 * mm});
            skCircle(sketch, "E8.0.39.3", {"center": v(57.68, 0.22) * mm, "radius": 0.62 * mm});
            skCircle(sketch, "E8.0.39.4", {"center": v(57.68, -3.03) * mm, "radius": 0.62 * mm});
            skCircle(sketch, "E8.0.39.5", {"center": v(57.68, -6.28) * mm, "radius": 0.62 * mm});
            skCircle(sketch, "E8.0.40.0", {"center": v(60.93, 9.97) * mm, "radius": 0.62 * mm});
            skCircle(sketch, "E8.0.40.1", {"center": v(60.93, 6.72) * mm, "radius": 0.62 * mm});
            skCircle(sketch, "E8.0.40.2", {"center": v(60.93, 3.47) * mm, "radius": 0.62 * mm});
            skCircle(sketch, "E8.0.40.3", {"center": v(60.93, 0.22) * mm, "radius": 0.62 * mm});
            skCircle(sketch, "E8.0.40.4", {"center": v(60.93, -3.03) * mm, "radius": 0.62 * mm});
            skCircle(sketch, "E8.0.40.5", {"center": v(60.93, -6.28) * mm, "radius": 0.62 * mm});
            skCircle(sketch, "E8.0.41.0", {"center": v(64.18, 9.97) * mm, "radius": 0.62 * mm});
            skCircle(sketch, "E8.0.41.1", {"center": v(64.18, 6.72) * mm, "radius": 0.62 * mm});
            skCircle(sketch, "E8.0.41.2", {"center": v(64.18, 3.47) * mm, "radius": 0.62 * mm});
            skCircle(sketch, "E8.0.41.3", {"center": v(64.18, 0.22) * mm, "radius": 0.62 * mm});
            skCircle(sketch, "E8.0.41.4", {"center": v(64.18, -3.03) * mm, "radius": 0.62 * mm});
            skCircle(sketch, "E8.0.41.5", {"center": v(64.18, -6.28) * mm, "radius": 0.62 * mm});
            skCircle(sketch, "E8.0.42.0", {"center": v(67.43, 9.97) * mm, "radius": 0.62 * mm});
            skCircle(sketch, "E8.0.42.1", {"center": v(67.43, 6.72) * mm, "radius": 0.62 * mm});
            skCircle(sketch, "E8.0.42.2", {"center": v(67.43, 3.47) * mm, "radius": 0.62 * mm});
            skCircle(sketch, "E8.0.42.3", {"center": v(67.43, 0.22) * mm, "radius": 0.62 * mm});
            skCircle(sketch, "E8.0.42.4", {"center": v(67.43, -3.03) * mm, "radius": 0.62 * mm});
            skCircle(sketch, "E8.0.42.5", {"center": v(67.43, -6.28) * mm, "radius": 0.62 * mm});
            skCircle(sketch, "E8.0.43.0", {"center": v(70.68, 9.97) * mm, "radius": 0.62 * mm});
            skCircle(sketch, "E8.0.43.1", {"center": v(70.68, 6.72) * mm, "radius": 0.62 * mm});
            skCircle(sketch, "E8.0.43.2", {"center": v(70.68, 3.47) * mm, "radius": 0.62 * mm});
            skCircle(sketch, "E8.0.43.3", {"center": v(70.68, 0.22) * mm, "radius": 0.62 * mm});
            skCircle(sketch, "E8.0.43.4", {"center": v(70.68, -3.03) * mm, "radius": 0.62 * mm});
            skCircle(sketch, "E8.0.43.5", {"center": v(70.68, -6.28) * mm, "radius": 0.62 * mm});
            skCircle(sketch, "E8.0.44.0", {"center": v(73.93, 9.97) * mm, "radius": 0.62 * mm});
            skCircle(sketch, "E8.0.44.1", {"center": v(73.93, 6.72) * mm, "radius": 0.62 * mm});
            skCircle(sketch, "E8.0.44.2", {"center": v(73.93, 3.47) * mm, "radius": 0.62 * mm});
            skCircle(sketch, "E8.0.44.3", {"center": v(73.93, 0.22) * mm, "radius": 0.62 * mm});
            skCircle(sketch, "E8.0.44.4", {"center": v(73.93, -3.03) * mm, "radius": 0.62 * mm});
            skCircle(sketch, "E8.0.44.5", {"center": v(73.93, -6.28) * mm, "radius": 0.62 * mm});
            skCircle(sketch, "E9.0.30.0", {"center": v(30.05, 8.34) * mm, "radius": 0.62 * mm});
            skCircle(sketch, "E9.0.30.1", {"center": v(30.05, 5.1) * mm, "radius": 0.62 * mm});
            skCircle(sketch, "E9.0.30.2", {"center": v(30.05, 1.84) * mm, "radius": 0.62 * mm});
            skCircle(sketch, "E9.0.30.3", {"center": v(30.05, -1.4) * mm, "radius": 0.62 * mm});
            skCircle(sketch, "E9.0.30.4", {"center": v(30.05, -4.66) * mm, "radius": 0.62 * mm});
            skCircle(sketch, "E9.0.30.5", {"center": v(30.05, -7.9) * mm, "radius": 0.62 * mm});
            skCircle(sketch, "E9.0.31.0", {"center": v(33.3, 8.34) * mm, "radius": 0.62 * mm});
            skCircle(sketch, "E9.0.31.1", {"center": v(33.3, 5.1) * mm, "radius": 0.62 * mm});
            skCircle(sketch, "E9.0.31.2", {"center": v(33.3, 1.84) * mm, "radius": 0.62 * mm});
            skCircle(sketch, "E9.0.31.3", {"center": v(33.3, -1.4) * mm, "radius": 0.62 * mm});
            skCircle(sketch, "E9.0.31.4", {"center": v(33.3, -4.66) * mm, "radius": 0.62 * mm});
            skCircle(sketch, "E9.0.31.5", {"center": v(33.3, -7.9) * mm, "radius": 0.62 * mm});
            skCircle(sketch, "E9.0.32.0", {"center": v(36.55, 8.34) * mm, "radius": 0.62 * mm});
            skCircle(sketch, "E9.0.32.1", {"center": v(36.55, 5.1) * mm, "radius": 0.62 * mm});
            skCircle(sketch, "E9.0.32.2", {"center": v(36.55, 1.84) * mm, "radius": 0.62 * mm});
            skCircle(sketch, "E9.0.32.3", {"center": v(36.55, -1.4) * mm, "radius": 0.62 * mm});
            skCircle(sketch, "E9.0.32.4", {"center": v(36.55, -4.66) * mm, "radius": 0.62 * mm});
            skCircle(sketch, "E9.0.32.5", {"center": v(36.55, -7.9) * mm, "radius": 0.62 * mm});
            skCircle(sketch, "E9.0.33.0", {"center": v(39.8, 8.34) * mm, "radius": 0.62 * mm});
            skCircle(sketch, "E9.0.33.1", {"center": v(39.8, 5.1) * mm, "radius": 0.62 * mm});
            skCircle(sketch, "E9.0.33.2", {"center": v(39.8, 1.84) * mm, "radius": 0.62 * mm});
            skCircle(sketch, "E9.0.33.3", {"center": v(39.8, -1.4) * mm, "radius": 0.62 * mm});
            skCircle(sketch, "E9.0.33.4", {"center": v(39.8, -4.66) * mm, "radius": 0.62 * mm});
            skCircle(sketch, "E9.0.33.5", {"center": v(39.8, -7.9) * mm, "radius": 0.62 * mm});
            skCircle(sketch, "E9.0.34.0", {"center": v(43.05, 8.34) * mm, "radius": 0.62 * mm});
            skCircle(sketch, "E9.0.34.1", {"center": v(43.05, 5.1) * mm, "radius": 0.62 * mm});
            skCircle(sketch, "E9.0.34.2", {"center": v(43.05, 1.84) * mm, "radius": 0.62 * mm});
            skCircle(sketch, "E9.0.34.3", {"center": v(43.05, -1.4) * mm, "radius": 0.62 * mm});
            skCircle(sketch, "E9.0.34.4", {"center": v(43.05, -4.66) * mm, "radius": 0.62 * mm});
            skCircle(sketch, "E9.0.34.5", {"center": v(43.05, -7.9) * mm, "radius": 0.62 * mm});
            skCircle(sketch, "E9.0.35.0", {"center": v(46.3, 8.34) * mm, "radius": 0.62 * mm});
            skCircle(sketch, "E9.0.35.1", {"center": v(46.3, 5.1) * mm, "radius": 0.62 * mm});
            skCircle(sketch, "E9.0.35.2", {"center": v(46.3, 1.84) * mm, "radius": 0.62 * mm});
            skCircle(sketch, "E9.0.35.3", {"center": v(46.3, -1.4) * mm, "radius": 0.62 * mm});
            skCircle(sketch, "E9.0.35.4", {"center": v(46.3, -4.66) * mm, "radius": 0.62 * mm});
            skCircle(sketch, "E9.0.35.5", {"center": v(46.3, -7.9) * mm, "radius": 0.62 * mm});
            skCircle(sketch, "E9.0.36.0", {"center": v(49.55, 8.34) * mm, "radius": 0.62 * mm});
            skCircle(sketch, "E9.0.36.1", {"center": v(49.55, 5.1) * mm, "radius": 0.62 * mm});
            skCircle(sketch, "E9.0.36.2", {"center": v(49.55, 1.84) * mm, "radius": 0.62 * mm});
            skCircle(sketch, "E9.0.36.3", {"center": v(49.55, -1.4) * mm, "radius": 0.62 * mm});
            skCircle(sketch, "E9.0.36.4", {"center": v(49.55, -4.66) * mm, "radius": 0.62 * mm});
            skCircle(sketch, "E9.0.36.5", {"center": v(49.55, -7.9) * mm, "radius": 0.62 * mm});
            skCircle(sketch, "E9.0.37.0", {"center": v(52.8, 8.34) * mm, "radius": 0.62 * mm});
            skCircle(sketch, "E9.0.37.1", {"center": v(52.8, 5.1) * mm, "radius": 0.62 * mm});
            skCircle(sketch, "E9.0.37.2", {"center": v(52.8, 1.84) * mm, "radius": 0.62 * mm});
            skCircle(sketch, "E9.0.37.3", {"center": v(52.8, -1.4) * mm, "radius": 0.62 * mm});
            skCircle(sketch, "E9.0.37.4", {"center": v(52.8, -4.66) * mm, "radius": 0.62 * mm});
            skCircle(sketch, "E9.0.37.5", {"center": v(52.8, -7.9) * mm, "radius": 0.62 * mm});
            skCircle(sketch, "E9.0.38.0", {"center": v(56.05, 8.34) * mm, "radius": 0.62 * mm});
            skCircle(sketch, "E9.0.38.1", {"center": v(56.05, 5.1) * mm, "radius": 0.62 * mm});
            skCircle(sketch, "E9.0.38.2", {"center": v(56.05, 1.84) * mm, "radius": 0.62 * mm});
            skCircle(sketch, "E9.0.38.3", {"center": v(56.05, -1.4) * mm, "radius": 0.62 * mm});
            skCircle(sketch, "E9.0.38.4", {"center": v(56.05, -4.66) * mm, "radius": 0.62 * mm});
            skCircle(sketch, "E9.0.38.5", {"center": v(56.05, -7.9) * mm, "radius": 0.62 * mm});
            skCircle(sketch, "E9.0.39.0", {"center": v(59.3, 8.34) * mm, "radius": 0.62 * mm});
            skCircle(sketch, "E9.0.39.1", {"center": v(59.3, 5.1) * mm, "radius": 0.62 * mm});
            skCircle(sketch, "E9.0.39.2", {"center": v(59.3, 1.84) * mm, "radius": 0.62 * mm});
            skCircle(sketch, "E9.0.39.3", {"center": v(59.3, -1.4) * mm, "radius": 0.62 * mm});
            skCircle(sketch, "E9.0.39.4", {"center": v(59.3, -4.66) * mm, "radius": 0.62 * mm});
            skCircle(sketch, "E9.0.39.5", {"center": v(59.3, -7.9) * mm, "radius": 0.62 * mm});
            skCircle(sketch, "E9.0.40.0", {"center": v(62.55, 8.34) * mm, "radius": 0.62 * mm});
            skCircle(sketch, "E9.0.40.1", {"center": v(62.55, 5.1) * mm, "radius": 0.62 * mm});
            skCircle(sketch, "E9.0.40.2", {"center": v(62.55, 1.84) * mm, "radius": 0.62 * mm});
            skCircle(sketch, "E9.0.40.3", {"center": v(62.55, -1.4) * mm, "radius": 0.62 * mm});
            skCircle(sketch, "E9.0.40.4", {"center": v(62.55, -4.66) * mm, "radius": 0.62 * mm});
            skCircle(sketch, "E9.0.40.5", {"center": v(62.55, -7.9) * mm, "radius": 0.62 * mm});
            skCircle(sketch, "E9.0.41.0", {"center": v(65.8, 8.34) * mm, "radius": 0.62 * mm});
            skCircle(sketch, "E9.0.41.1", {"center": v(65.8, 5.1) * mm, "radius": 0.62 * mm});
            skCircle(sketch, "E9.0.41.2", {"center": v(65.8, 1.84) * mm, "radius": 0.62 * mm});
            skCircle(sketch, "E9.0.41.3", {"center": v(65.8, -1.4) * mm, "radius": 0.62 * mm});
            skCircle(sketch, "E9.0.41.4", {"center": v(65.8, -4.66) * mm, "radius": 0.62 * mm});
            skCircle(sketch, "E9.0.41.5", {"center": v(65.8, -7.9) * mm, "radius": 0.62 * mm});
            skCircle(sketch, "E9.0.42.0", {"center": v(69.05, 8.34) * mm, "radius": 0.62 * mm});
            skCircle(sketch, "E9.0.42.1", {"center": v(69.05, 5.1) * mm, "radius": 0.62 * mm});
            skCircle(sketch, "E9.0.42.2", {"center": v(69.05, 1.84) * mm, "radius": 0.62 * mm});
            skCircle(sketch, "E9.0.42.3", {"center": v(69.05, -1.4) * mm, "radius": 0.62 * mm});
            skCircle(sketch, "E9.0.42.4", {"center": v(69.05, -4.66) * mm, "radius": 0.62 * mm});
            skCircle(sketch, "E9.0.42.5", {"center": v(69.05, -7.9) * mm, "radius": 0.62 * mm});
            skCircle(sketch, "E9.0.43.0", {"center": v(72.3, 8.34) * mm, "radius": 0.62 * mm});
            skCircle(sketch, "E9.0.43.1", {"center": v(72.3, 5.1) * mm, "radius": 0.62 * mm});
            skCircle(sketch, "E9.0.43.2", {"center": v(72.3, 1.84) * mm, "radius": 0.62 * mm});
            skCircle(sketch, "E9.0.43.3", {"center": v(72.3, -1.4) * mm, "radius": 0.62 * mm});
            skCircle(sketch, "E9.0.43.4", {"center": v(72.3, -4.66) * mm, "radius": 0.62 * mm});
            skCircle(sketch, "E9.0.43.5", {"center": v(72.3, -7.9) * mm, "radius": 0.62 * mm});
            skCircle(sketch, "E9.0.44.0", {"center": v(75.55, 8.34) * mm, "radius": 0.62 * mm});
            skCircle(sketch, "E9.0.44.1", {"center": v(75.55, 5.1) * mm, "radius": 0.62 * mm});
            skCircle(sketch, "E9.0.44.2", {"center": v(75.55, 1.84) * mm, "radius": 0.62 * mm});
            skCircle(sketch, "E9.0.44.3", {"center": v(75.55, -1.4) * mm, "radius": 0.62 * mm});
            skCircle(sketch, "E9.0.44.4", {"center": v(75.55, -4.66) * mm, "radius": 0.62 * mm});
            skCircle(sketch, "E9.0.44.5", {"center": v(75.55, -7.9) * mm, "radius": 0.62 * mm});
            skCircle(sketch, "E10.0.0.6", {"center": v(-69.07, -9.53) * mm, "radius": 0.62 * mm});
            skCircle(sketch, "E10.0.0.7", {"center": v(-69.07, -12.78) * mm, "radius": 0.62 * mm});
            skCircle(sketch, "E10.0.0.8", {"center": v(-69.07, -16.03) * mm, "radius": 0.62 * mm});
            skCircle(sketch, "E10.0.0.9", {"center": v(-69.07, -19.28) * mm, "radius": 0.62 * mm});
            skCircle(sketch, "E10.0.0.10", {"center": v(-69.07, -22.53) * mm, "radius": 0.62 * mm});
            skCircle(sketch, "E10.0.0.11", {"center": v(-69.07, -25.78) * mm, "radius": 0.62 * mm});
            skCircle(sketch, "E10.0.0.12", {"center": v(-69.07, -29.03) * mm, "radius": 0.62 * mm});
            skCircle(sketch, "E10.0.0.13", {"center": v(-69.07, -32.28) * mm, "radius": 0.62 * mm});
            skCircle(sketch, "E10.0.0.14", {"center": v(-69.07, -35.53) * mm, "radius": 0.62 * mm});
            skCircle(sketch, "E10.0.1.6", {"center": v(-65.82, -9.53) * mm, "radius": 0.62 * mm});
            skCircle(sketch, "E10.0.1.7", {"center": v(-65.82, -12.78) * mm, "radius": 0.62 * mm});
            skCircle(sketch, "E10.0.1.8", {"center": v(-65.82, -16.03) * mm, "radius": 0.62 * mm});
            skCircle(sketch, "E10.0.1.9", {"center": v(-65.82, -19.28) * mm, "radius": 0.62 * mm});
            skCircle(sketch, "E10.0.1.10", {"center": v(-65.82, -22.53) * mm, "radius": 0.62 * mm});
            skCircle(sketch, "E10.0.1.11", {"center": v(-65.82, -25.78) * mm, "radius": 0.62 * mm});
            skCircle(sketch, "E10.0.1.12", {"center": v(-65.82, -29.03) * mm, "radius": 0.62 * mm});
            skCircle(sketch, "E10.0.1.13", {"center": v(-65.82, -32.28) * mm, "radius": 0.62 * mm});
            skCircle(sketch, "E10.0.1.14", {"center": v(-65.82, -35.53) * mm, "radius": 0.62 * mm});
            skCircle(sketch, "E10.0.2.6", {"center": v(-62.57, -9.53) * mm, "radius": 0.62 * mm});
            skCircle(sketch, "E10.0.2.7", {"center": v(-62.57, -12.78) * mm, "radius": 0.62 * mm});
            skCircle(sketch, "E10.0.2.8", {"center": v(-62.57, -16.03) * mm, "radius": 0.62 * mm});
            skCircle(sketch, "E10.0.2.9", {"center": v(-62.57, -19.28) * mm, "radius": 0.62 * mm});
            skCircle(sketch, "E10.0.2.10", {"center": v(-62.57, -22.53) * mm, "radius": 0.62 * mm});
            skCircle(sketch, "E10.0.2.11", {"center": v(-62.57, -25.78) * mm, "radius": 0.62 * mm});
            skCircle(sketch, "E10.0.2.12", {"center": v(-62.57, -29.03) * mm, "radius": 0.62 * mm});
            skCircle(sketch, "E10.0.2.13", {"center": v(-62.57, -32.28) * mm, "radius": 0.62 * mm});
            skCircle(sketch, "E10.0.2.14", {"center": v(-62.57, -35.53) * mm, "radius": 0.62 * mm});
            skCircle(sketch, "E10.0.3.6", {"center": v(-59.32, -9.53) * mm, "radius": 0.62 * mm});
            skCircle(sketch, "E10.0.3.7", {"center": v(-59.32, -12.78) * mm, "radius": 0.62 * mm});
            skCircle(sketch, "E10.0.3.8", {"center": v(-59.32, -16.03) * mm, "radius": 0.62 * mm});
            skCircle(sketch, "E10.0.3.9", {"center": v(-59.32, -19.28) * mm, "radius": 0.62 * mm});
            skCircle(sketch, "E10.0.3.10", {"center": v(-59.32, -22.53) * mm, "radius": 0.62 * mm});
            skCircle(sketch, "E10.0.3.11", {"center": v(-59.32, -25.78) * mm, "radius": 0.62 * mm});
            skCircle(sketch, "E10.0.3.12", {"center": v(-59.32, -29.03) * mm, "radius": 0.62 * mm});
            skCircle(sketch, "E10.0.3.13", {"center": v(-59.32, -32.28) * mm, "radius": 0.62 * mm});
            skCircle(sketch, "E10.0.3.14", {"center": v(-59.32, -35.53) * mm, "radius": 0.62 * mm});
            skCircle(sketch, "E10.0.4.6", {"center": v(-56.07, -9.53) * mm, "radius": 0.62 * mm});
            skCircle(sketch, "E10.0.4.7", {"center": v(-56.07, -12.78) * mm, "radius": 0.62 * mm});
            skCircle(sketch, "E10.0.4.8", {"center": v(-56.07, -16.03) * mm, "radius": 0.62 * mm});
            skCircle(sketch, "E10.0.4.9", {"center": v(-56.07, -19.28) * mm, "radius": 0.62 * mm});
            skCircle(sketch, "E10.0.4.10", {"center": v(-56.07, -22.53) * mm, "radius": 0.62 * mm});
            skCircle(sketch, "E10.0.4.11", {"center": v(-56.07, -25.78) * mm, "radius": 0.62 * mm});
            skCircle(sketch, "E10.0.4.12", {"center": v(-56.07, -29.03) * mm, "radius": 0.62 * mm});
            skCircle(sketch, "E10.0.4.13", {"center": v(-56.07, -32.28) * mm, "radius": 0.62 * mm});
            skCircle(sketch, "E10.0.4.14", {"center": v(-56.07, -35.53) * mm, "radius": 0.62 * mm});
            skCircle(sketch, "E10.0.5.6", {"center": v(-52.82, -9.53) * mm, "radius": 0.62 * mm});
            skCircle(sketch, "E10.0.5.7", {"center": v(-52.82, -12.78) * mm, "radius": 0.62 * mm});
            skCircle(sketch, "E10.0.5.8", {"center": v(-52.82, -16.03) * mm, "radius": 0.62 * mm});
            skCircle(sketch, "E10.0.5.9", {"center": v(-52.82, -19.28) * mm, "radius": 0.62 * mm});
            skCircle(sketch, "E10.0.5.10", {"center": v(-52.82, -22.53) * mm, "radius": 0.62 * mm});
            skCircle(sketch, "E10.0.5.11", {"center": v(-52.82, -25.78) * mm, "radius": 0.62 * mm});
            skCircle(sketch, "E10.0.5.12", {"center": v(-52.82, -29.03) * mm, "radius": 0.62 * mm});
            skCircle(sketch, "E10.0.5.13", {"center": v(-52.82, -32.28) * mm, "radius": 0.62 * mm});
            skCircle(sketch, "E10.0.5.14", {"center": v(-52.82, -35.53) * mm, "radius": 0.62 * mm});
            skCircle(sketch, "E10.0.6.6", {"center": v(-49.57, -9.53) * mm, "radius": 0.62 * mm});
            skCircle(sketch, "E10.0.6.7", {"center": v(-49.57, -12.78) * mm, "radius": 0.62 * mm});
            skCircle(sketch, "E10.0.6.8", {"center": v(-49.57, -16.03) * mm, "radius": 0.62 * mm});
            skCircle(sketch, "E10.0.6.9", {"center": v(-49.57, -19.28) * mm, "radius": 0.62 * mm});
            skCircle(sketch, "E10.0.6.10", {"center": v(-49.57, -22.53) * mm, "radius": 0.62 * mm});
            skCircle(sketch, "E10.0.6.11", {"center": v(-49.57, -25.78) * mm, "radius": 0.62 * mm});
            skCircle(sketch, "E10.0.6.12", {"center": v(-49.57, -29.03) * mm, "radius": 0.62 * mm});
            skCircle(sketch, "E10.0.6.13", {"center": v(-49.57, -32.28) * mm, "radius": 0.62 * mm});
            skCircle(sketch, "E10.0.6.14", {"center": v(-49.57, -35.53) * mm, "radius": 0.62 * mm});
            skCircle(sketch, "E10.0.7.6", {"center": v(-46.32, -9.53) * mm, "radius": 0.62 * mm});
            skCircle(sketch, "E10.0.7.7", {"center": v(-46.32, -12.78) * mm, "radius": 0.62 * mm});
            skCircle(sketch, "E10.0.7.8", {"center": v(-46.32, -16.03) * mm, "radius": 0.62 * mm});
            skCircle(sketch, "E10.0.7.9", {"center": v(-46.32, -19.28) * mm, "radius": 0.62 * mm});
            skCircle(sketch, "E10.0.7.10", {"center": v(-46.32, -22.53) * mm, "radius": 0.62 * mm});
            skCircle(sketch, "E10.0.7.11", {"center": v(-46.32, -25.78) * mm, "radius": 0.62 * mm});
            skCircle(sketch, "E10.0.7.12", {"center": v(-46.32, -29.03) * mm, "radius": 0.62 * mm});
            skCircle(sketch, "E10.0.7.13", {"center": v(-46.32, -32.28) * mm, "radius": 0.62 * mm});
            skCircle(sketch, "E10.0.7.14", {"center": v(-46.32, -35.53) * mm, "radius": 0.62 * mm});
            skCircle(sketch, "E10.0.8.6", {"center": v(-43.07, -9.53) * mm, "radius": 0.62 * mm});
            skCircle(sketch, "E10.0.8.7", {"center": v(-43.07, -12.78) * mm, "radius": 0.62 * mm});
            skCircle(sketch, "E10.0.8.8", {"center": v(-43.07, -16.03) * mm, "radius": 0.62 * mm});
            skCircle(sketch, "E10.0.8.9", {"center": v(-43.07, -19.28) * mm, "radius": 0.62 * mm});
            skCircle(sketch, "E10.0.8.10", {"center": v(-43.07, -22.53) * mm, "radius": 0.62 * mm});
            skCircle(sketch, "E10.0.8.11", {"center": v(-43.07, -25.78) * mm, "radius": 0.62 * mm});
            skCircle(sketch, "E10.0.8.12", {"center": v(-43.07, -29.03) * mm, "radius": 0.62 * mm});
            skCircle(sketch, "E10.0.8.13", {"center": v(-43.07, -32.28) * mm, "radius": 0.62 * mm});
            skCircle(sketch, "E10.0.8.14", {"center": v(-43.07, -35.53) * mm, "radius": 0.62 * mm});
            skCircle(sketch, "E10.0.9.6", {"center": v(-39.82, -9.53) * mm, "radius": 0.62 * mm});
            skCircle(sketch, "E10.0.9.7", {"center": v(-39.82, -12.78) * mm, "radius": 0.62 * mm});
            skCircle(sketch, "E10.0.9.8", {"center": v(-39.82, -16.03) * mm, "radius": 0.62 * mm});
            skCircle(sketch, "E10.0.9.9", {"center": v(-39.82, -19.28) * mm, "radius": 0.62 * mm});
            skCircle(sketch, "E10.0.9.10", {"center": v(-39.82, -22.53) * mm, "radius": 0.62 * mm});
            skCircle(sketch, "E10.0.9.11", {"center": v(-39.82, -25.78) * mm, "radius": 0.62 * mm});
            skCircle(sketch, "E10.0.9.12", {"center": v(-39.82, -29.03) * mm, "radius": 0.62 * mm});
            skCircle(sketch, "E10.0.9.13", {"center": v(-39.82, -32.28) * mm, "radius": 0.62 * mm});
            skCircle(sketch, "E10.0.9.14", {"center": v(-39.82, -35.53) * mm, "radius": 0.62 * mm});
            skCircle(sketch, "E10.0.10.6", {"center": v(-36.57, -9.53) * mm, "radius": 0.62 * mm});
            skCircle(sketch, "E10.0.10.7", {"center": v(-36.57, -12.78) * mm, "radius": 0.62 * mm});
            skCircle(sketch, "E10.0.10.8", {"center": v(-36.57, -16.03) * mm, "radius": 0.62 * mm});
            skCircle(sketch, "E10.0.10.9", {"center": v(-36.57, -19.28) * mm, "radius": 0.62 * mm});
            skCircle(sketch, "E10.0.10.10", {"center": v(-36.57, -22.53) * mm, "radius": 0.62 * mm});
            skCircle(sketch, "E10.0.10.11", {"center": v(-36.57, -25.78) * mm, "radius": 0.62 * mm});
            skCircle(sketch, "E10.0.10.12", {"center": v(-36.57, -29.03) * mm, "radius": 0.62 * mm});
            skCircle(sketch, "E10.0.10.13", {"center": v(-36.57, -32.28) * mm, "radius": 0.62 * mm});
            skCircle(sketch, "E10.0.10.14", {"center": v(-36.57, -35.53) * mm, "radius": 0.62 * mm});
            skCircle(sketch, "E10.0.11.6", {"center": v(-33.32, -9.53) * mm, "radius": 0.62 * mm});
            skCircle(sketch, "E10.0.11.7", {"center": v(-33.32, -12.78) * mm, "radius": 0.62 * mm});
            skCircle(sketch, "E10.0.11.8", {"center": v(-33.32, -16.03) * mm, "radius": 0.62 * mm});
            skCircle(sketch, "E10.0.11.9", {"center": v(-33.32, -19.28) * mm, "radius": 0.62 * mm});
            skCircle(sketch, "E10.0.11.10", {"center": v(-33.32, -22.53) * mm, "radius": 0.62 * mm});
            skCircle(sketch, "E10.0.11.11", {"center": v(-33.32, -25.78) * mm, "radius": 0.62 * mm});
            skCircle(sketch, "E10.0.11.12", {"center": v(-33.32, -29.03) * mm, "radius": 0.62 * mm});
            skCircle(sketch, "E10.0.11.13", {"center": v(-33.32, -32.28) * mm, "radius": 0.62 * mm});
            skCircle(sketch, "E10.0.11.14", {"center": v(-33.32, -35.53) * mm, "radius": 0.62 * mm});
            skCircle(sketch, "E10.0.12.6", {"center": v(-30.07, -9.53) * mm, "radius": 0.62 * mm});
            skCircle(sketch, "E10.0.12.7", {"center": v(-30.07, -12.78) * mm, "radius": 0.62 * mm});
            skCircle(sketch, "E10.0.12.8", {"center": v(-30.07, -16.03) * mm, "radius": 0.62 * mm});
            skCircle(sketch, "E10.0.12.9", {"center": v(-30.07, -19.28) * mm, "radius": 0.62 * mm});
            skCircle(sketch, "E10.0.12.10", {"center": v(-30.07, -22.53) * mm, "radius": 0.62 * mm});
            skCircle(sketch, "E10.0.12.11", {"center": v(-30.07, -25.78) * mm, "radius": 0.62 * mm});
            skCircle(sketch, "E10.0.12.12", {"center": v(-30.07, -29.03) * mm, "radius": 0.62 * mm});
            skCircle(sketch, "E10.0.12.13", {"center": v(-30.07, -32.28) * mm, "radius": 0.62 * mm});
            skCircle(sketch, "E10.0.12.14", {"center": v(-30.07, -35.53) * mm, "radius": 0.62 * mm});
            skCircle(sketch, "E10.0.13.6", {"center": v(-26.82, -9.53) * mm, "radius": 0.62 * mm});
            skCircle(sketch, "E10.0.13.7", {"center": v(-26.82, -12.78) * mm, "radius": 0.62 * mm});
            skCircle(sketch, "E10.0.13.8", {"center": v(-26.82, -16.03) * mm, "radius": 0.62 * mm});
            skCircle(sketch, "E10.0.13.9", {"center": v(-26.82, -19.28) * mm, "radius": 0.62 * mm});
            skCircle(sketch, "E10.0.13.10", {"center": v(-26.82, -22.53) * mm, "radius": 0.62 * mm});
            skCircle(sketch, "E10.0.13.11", {"center": v(-26.82, -25.78) * mm, "radius": 0.62 * mm});
            skCircle(sketch, "E10.0.13.12", {"center": v(-26.82, -29.03) * mm, "radius": 0.62 * mm});
            skCircle(sketch, "E10.0.13.13", {"center": v(-26.82, -32.28) * mm, "radius": 0.62 * mm});
            skCircle(sketch, "E10.0.13.14", {"center": v(-26.82, -35.53) * mm, "radius": 0.62 * mm});
            skCircle(sketch, "E10.0.14.6", {"center": v(-23.57, -9.53) * mm, "radius": 0.62 * mm});
            skCircle(sketch, "E10.0.14.7", {"center": v(-23.57, -12.78) * mm, "radius": 0.62 * mm});
            skCircle(sketch, "E10.0.14.8", {"center": v(-23.57, -16.03) * mm, "radius": 0.62 * mm});
            skCircle(sketch, "E10.0.14.9", {"center": v(-23.57, -19.28) * mm, "radius": 0.62 * mm});
            skCircle(sketch, "E10.0.14.10", {"center": v(-23.57, -22.53) * mm, "radius": 0.62 * mm});
            skCircle(sketch, "E10.0.14.11", {"center": v(-23.57, -25.78) * mm, "radius": 0.62 * mm});
            skCircle(sketch, "E10.0.14.12", {"center": v(-23.57, -29.03) * mm, "radius": 0.62 * mm});
            skCircle(sketch, "E10.0.14.13", {"center": v(-23.57, -32.28) * mm, "radius": 0.62 * mm});
            skCircle(sketch, "E10.0.14.14", {"center": v(-23.57, -35.53) * mm, "radius": 0.62 * mm});
            skCircle(sketch, "E10.0.15.6", {"center": v(-20.32, -9.53) * mm, "radius": 0.62 * mm});
            skCircle(sketch, "E10.0.15.7", {"center": v(-20.32, -12.78) * mm, "radius": 0.62 * mm});
            skCircle(sketch, "E10.0.15.8", {"center": v(-20.32, -16.03) * mm, "radius": 0.62 * mm});
            skCircle(sketch, "E10.0.15.9", {"center": v(-20.32, -19.28) * mm, "radius": 0.62 * mm});
            skCircle(sketch, "E10.0.15.10", {"center": v(-20.32, -22.53) * mm, "radius": 0.62 * mm});
            skCircle(sketch, "E10.0.15.11", {"center": v(-20.32, -25.78) * mm, "radius": 0.62 * mm});
            skCircle(sketch, "E10.0.15.12", {"center": v(-20.32, -29.03) * mm, "radius": 0.62 * mm});
            skCircle(sketch, "E10.0.15.13", {"center": v(-20.32, -32.28) * mm, "radius": 0.62 * mm});
            skCircle(sketch, "E10.0.15.14", {"center": v(-20.32, -35.53) * mm, "radius": 0.62 * mm});
            skCircle(sketch, "E10.0.16.6", {"center": v(-17.07, -9.53) * mm, "radius": 0.62 * mm});
            skCircle(sketch, "E10.0.16.7", {"center": v(-17.07, -12.78) * mm, "radius": 0.62 * mm});
            skCircle(sketch, "E10.0.16.8", {"center": v(-17.07, -16.03) * mm, "radius": 0.62 * mm});
            skCircle(sketch, "E10.0.16.9", {"center": v(-17.07, -19.28) * mm, "radius": 0.62 * mm});
            skCircle(sketch, "E10.0.16.10", {"center": v(-17.07, -22.53) * mm, "radius": 0.62 * mm});
            skCircle(sketch, "E10.0.16.11", {"center": v(-17.07, -25.78) * mm, "radius": 0.62 * mm});
            skCircle(sketch, "E10.0.16.12", {"center": v(-17.07, -29.03) * mm, "radius": 0.62 * mm});
            skCircle(sketch, "E10.0.16.13", {"center": v(-17.07, -32.28) * mm, "radius": 0.62 * mm});
            skCircle(sketch, "E10.0.16.14", {"center": v(-17.07, -35.53) * mm, "radius": 0.62 * mm});
            skCircle(sketch, "E10.0.17.6", {"center": v(-13.82, -9.53) * mm, "radius": 0.62 * mm});
            skCircle(sketch, "E10.0.17.7", {"center": v(-13.82, -12.78) * mm, "radius": 0.62 * mm});
            skCircle(sketch, "E10.0.17.8", {"center": v(-13.82, -16.03) * mm, "radius": 0.62 * mm});
            skCircle(sketch, "E10.0.17.9", {"center": v(-13.82, -19.28) * mm, "radius": 0.62 * mm});
            skCircle(sketch, "E10.0.17.10", {"center": v(-13.82, -22.53) * mm, "radius": 0.62 * mm});
            skCircle(sketch, "E10.0.17.11", {"center": v(-13.82, -25.78) * mm, "radius": 0.62 * mm});
            skCircle(sketch, "E10.0.17.12", {"center": v(-13.82, -29.03) * mm, "radius": 0.62 * mm});
            skCircle(sketch, "E10.0.17.13", {"center": v(-13.82, -32.28) * mm, "radius": 0.62 * mm});
            skCircle(sketch, "E10.0.17.14", {"center": v(-13.82, -35.53) * mm, "radius": 0.62 * mm});
            skCircle(sketch, "E10.0.18.6", {"center": v(-10.57, -9.53) * mm, "radius": 0.62 * mm});
            skCircle(sketch, "E10.0.18.7", {"center": v(-10.57, -12.78) * mm, "radius": 0.62 * mm});
            skCircle(sketch, "E10.0.18.8", {"center": v(-10.57, -16.03) * mm, "radius": 0.62 * mm});
            skCircle(sketch, "E10.0.18.9", {"center": v(-10.57, -19.28) * mm, "radius": 0.62 * mm});
            skCircle(sketch, "E10.0.18.10", {"center": v(-10.57, -22.53) * mm, "radius": 0.62 * mm});
            skCircle(sketch, "E10.0.18.11", {"center": v(-10.57, -25.78) * mm, "radius": 0.62 * mm});
            skCircle(sketch, "E10.0.18.12", {"center": v(-10.57, -29.03) * mm, "radius": 0.62 * mm});
            skCircle(sketch, "E10.0.18.13", {"center": v(-10.57, -32.28) * mm, "radius": 0.62 * mm});
            skCircle(sketch, "E10.0.18.14", {"center": v(-10.57, -35.53) * mm, "radius": 0.62 * mm});
            skCircle(sketch, "E10.0.19.6", {"center": v(-7.32, -9.53) * mm, "radius": 0.62 * mm});
            skCircle(sketch, "E10.0.19.7", {"center": v(-7.32, -12.78) * mm, "radius": 0.62 * mm});
            skCircle(sketch, "E10.0.19.8", {"center": v(-7.32, -16.03) * mm, "radius": 0.62 * mm});
            skCircle(sketch, "E10.0.19.9", {"center": v(-7.32, -19.28) * mm, "radius": 0.62 * mm});
            skCircle(sketch, "E10.0.19.10", {"center": v(-7.32, -22.53) * mm, "radius": 0.62 * mm});
            skCircle(sketch, "E10.0.19.11", {"center": v(-7.32, -25.78) * mm, "radius": 0.62 * mm});
            skCircle(sketch, "E10.0.19.12", {"center": v(-7.32, -29.03) * mm, "radius": 0.62 * mm});
            skCircle(sketch, "E10.0.19.13", {"center": v(-7.32, -32.28) * mm, "radius": 0.62 * mm});
            skCircle(sketch, "E10.0.19.14", {"center": v(-7.32, -35.53) * mm, "radius": 0.62 * mm});
            skCircle(sketch, "E10.0.20.6", {"center": v(-4.07, -9.53) * mm, "radius": 0.62 * mm});
            skCircle(sketch, "E10.0.20.7", {"center": v(-4.07, -12.78) * mm, "radius": 0.62 * mm});
            skCircle(sketch, "E10.0.20.8", {"center": v(-4.07, -16.03) * mm, "radius": 0.62 * mm});
            skCircle(sketch, "E10.0.20.9", {"center": v(-4.07, -19.28) * mm, "radius": 0.62 * mm});
            skCircle(sketch, "E10.0.20.10", {"center": v(-4.07, -22.53) * mm, "radius": 0.62 * mm});
            skCircle(sketch, "E10.0.20.11", {"center": v(-4.07, -25.78) * mm, "radius": 0.62 * mm});
            skCircle(sketch, "E10.0.20.12", {"center": v(-4.07, -29.03) * mm, "radius": 0.62 * mm});
            skCircle(sketch, "E10.0.20.13", {"center": v(-4.07, -32.28) * mm, "radius": 0.62 * mm});
            skCircle(sketch, "E10.0.20.14", {"center": v(-4.07, -35.53) * mm, "radius": 0.62 * mm});
            skCircle(sketch, "E10.0.21.6", {"center": v(-0.82, -9.53) * mm, "radius": 0.62 * mm});
            skCircle(sketch, "E10.0.21.7", {"center": v(-0.82, -12.78) * mm, "radius": 0.62 * mm});
            skCircle(sketch, "E10.0.21.8", {"center": v(-0.82, -16.03) * mm, "radius": 0.62 * mm});
            skCircle(sketch, "E10.0.21.9", {"center": v(-0.82, -19.28) * mm, "radius": 0.62 * mm});
            skCircle(sketch, "E10.0.21.10", {"center": v(-0.82, -22.53) * mm, "radius": 0.62 * mm});
            skCircle(sketch, "E10.0.21.11", {"center": v(-0.82, -25.78) * mm, "radius": 0.62 * mm});
            skCircle(sketch, "E10.0.21.12", {"center": v(-0.82, -29.03) * mm, "radius": 0.62 * mm});
            skCircle(sketch, "E10.0.21.13", {"center": v(-0.82, -32.28) * mm, "radius": 0.62 * mm});
            skCircle(sketch, "E10.0.21.14", {"center": v(-0.82, -35.53) * mm, "radius": 0.62 * mm});
            skCircle(sketch, "E10.0.22.6", {"center": v(2.43, -9.53) * mm, "radius": 0.62 * mm});
            skCircle(sketch, "E10.0.22.7", {"center": v(2.43, -12.78) * mm, "radius": 0.62 * mm});
            skCircle(sketch, "E10.0.22.8", {"center": v(2.43, -16.03) * mm, "radius": 0.62 * mm});
            skCircle(sketch, "E10.0.22.9", {"center": v(2.43, -19.28) * mm, "radius": 0.62 * mm});
            skCircle(sketch, "E10.0.22.10", {"center": v(2.43, -22.53) * mm, "radius": 0.62 * mm});
            skCircle(sketch, "E10.0.22.11", {"center": v(2.43, -25.78) * mm, "radius": 0.62 * mm});
            skCircle(sketch, "E10.0.22.12", {"center": v(2.43, -29.03) * mm, "radius": 0.62 * mm});
            skCircle(sketch, "E10.0.22.13", {"center": v(2.43, -32.28) * mm, "radius": 0.62 * mm});
            skCircle(sketch, "E10.0.22.14", {"center": v(2.43, -35.53) * mm, "radius": 0.62 * mm});
            skCircle(sketch, "E10.0.23.6", {"center": v(5.68, -9.53) * mm, "radius": 0.62 * mm});
            skCircle(sketch, "E10.0.23.7", {"center": v(5.68, -12.78) * mm, "radius": 0.62 * mm});
            skCircle(sketch, "E10.0.23.8", {"center": v(5.68, -16.03) * mm, "radius": 0.62 * mm});
            skCircle(sketch, "E10.0.23.9", {"center": v(5.68, -19.28) * mm, "radius": 0.62 * mm});
            skCircle(sketch, "E10.0.23.10", {"center": v(5.68, -22.53) * mm, "radius": 0.62 * mm});
            skCircle(sketch, "E10.0.23.11", {"center": v(5.68, -25.78) * mm, "radius": 0.62 * mm});
            skCircle(sketch, "E10.0.23.12", {"center": v(5.68, -29.03) * mm, "radius": 0.62 * mm});
            skCircle(sketch, "E10.0.23.13", {"center": v(5.68, -32.28) * mm, "radius": 0.62 * mm});
            skCircle(sketch, "E10.0.23.14", {"center": v(5.68, -35.53) * mm, "radius": 0.62 * mm});
            skCircle(sketch, "E10.0.24.6", {"center": v(8.93, -9.53) * mm, "radius": 0.62 * mm});
            skCircle(sketch, "E10.0.24.7", {"center": v(8.93, -12.78) * mm, "radius": 0.62 * mm});
            skCircle(sketch, "E10.0.24.8", {"center": v(8.93, -16.03) * mm, "radius": 0.62 * mm});
            skCircle(sketch, "E10.0.24.9", {"center": v(8.93, -19.28) * mm, "radius": 0.62 * mm});
            skCircle(sketch, "E10.0.24.10", {"center": v(8.93, -22.53) * mm, "radius": 0.62 * mm});
            skCircle(sketch, "E10.0.24.11", {"center": v(8.93, -25.78) * mm, "radius": 0.62 * mm});
            skCircle(sketch, "E10.0.24.12", {"center": v(8.93, -29.03) * mm, "radius": 0.62 * mm});
            skCircle(sketch, "E10.0.24.13", {"center": v(8.93, -32.28) * mm, "radius": 0.62 * mm});
            skCircle(sketch, "E10.0.24.14", {"center": v(8.93, -35.53) * mm, "radius": 0.62 * mm});
            skCircle(sketch, "E10.0.25.6", {"center": v(12.18, -9.53) * mm, "radius": 0.62 * mm});
            skCircle(sketch, "E10.0.25.7", {"center": v(12.18, -12.78) * mm, "radius": 0.62 * mm});
            skCircle(sketch, "E10.0.25.8", {"center": v(12.18, -16.03) * mm, "radius": 0.62 * mm});
            skCircle(sketch, "E10.0.25.9", {"center": v(12.18, -19.28) * mm, "radius": 0.62 * mm});
            skCircle(sketch, "E10.0.25.10", {"center": v(12.18, -22.53) * mm, "radius": 0.62 * mm});
            skCircle(sketch, "E10.0.25.11", {"center": v(12.18, -25.78) * mm, "radius": 0.62 * mm});
            skCircle(sketch, "E10.0.25.12", {"center": v(12.18, -29.03) * mm, "radius": 0.62 * mm});
            skCircle(sketch, "E10.0.25.13", {"center": v(12.18, -32.28) * mm, "radius": 0.62 * mm});
            skCircle(sketch, "E10.0.25.14", {"center": v(12.18, -35.53) * mm, "radius": 0.62 * mm});
            skCircle(sketch, "E10.0.26.6", {"center": v(15.43, -9.53) * mm, "radius": 0.62 * mm});
            skCircle(sketch, "E10.0.26.7", {"center": v(15.43, -12.78) * mm, "radius": 0.62 * mm});
            skCircle(sketch, "E10.0.26.8", {"center": v(15.43, -16.03) * mm, "radius": 0.62 * mm});
            skCircle(sketch, "E10.0.26.9", {"center": v(15.43, -19.28) * mm, "radius": 0.62 * mm});
            skCircle(sketch, "E10.0.26.10", {"center": v(15.43, -22.53) * mm, "radius": 0.62 * mm});
            skCircle(sketch, "E10.0.26.11", {"center": v(15.43, -25.78) * mm, "radius": 0.62 * mm});
            skCircle(sketch, "E10.0.26.12", {"center": v(15.43, -29.03) * mm, "radius": 0.62 * mm});
            skCircle(sketch, "E10.0.26.13", {"center": v(15.43, -32.28) * mm, "radius": 0.62 * mm});
            skCircle(sketch, "E10.0.26.14", {"center": v(15.43, -35.53) * mm, "radius": 0.62 * mm});
            skCircle(sketch, "E10.0.27.6", {"center": v(18.68, -9.53) * mm, "radius": 0.62 * mm});
            skCircle(sketch, "E10.0.27.7", {"center": v(18.68, -12.78) * mm, "radius": 0.62 * mm});
            skCircle(sketch, "E10.0.27.8", {"center": v(18.68, -16.03) * mm, "radius": 0.62 * mm});
            skCircle(sketch, "E10.0.27.9", {"center": v(18.68, -19.28) * mm, "radius": 0.62 * mm});
            skCircle(sketch, "E10.0.27.10", {"center": v(18.68, -22.53) * mm, "radius": 0.62 * mm});
            skCircle(sketch, "E10.0.27.11", {"center": v(18.68, -25.78) * mm, "radius": 0.62 * mm});
            skCircle(sketch, "E10.0.27.12", {"center": v(18.68, -29.03) * mm, "radius": 0.62 * mm});
            skCircle(sketch, "E10.0.27.13", {"center": v(18.68, -32.28) * mm, "radius": 0.62 * mm});
            skCircle(sketch, "E10.0.27.14", {"center": v(18.68, -35.53) * mm, "radius": 0.62 * mm});
            skCircle(sketch, "E10.0.28.6", {"center": v(21.93, -9.53) * mm, "radius": 0.62 * mm});
            skCircle(sketch, "E10.0.28.7", {"center": v(21.93, -12.78) * mm, "radius": 0.62 * mm});
            skCircle(sketch, "E10.0.28.8", {"center": v(21.93, -16.03) * mm, "radius": 0.62 * mm});
            skCircle(sketch, "E10.0.28.9", {"center": v(21.93, -19.28) * mm, "radius": 0.62 * mm});
            skCircle(sketch, "E10.0.28.10", {"center": v(21.93, -22.53) * mm, "radius": 0.62 * mm});
            skCircle(sketch, "E10.0.28.11", {"center": v(21.93, -25.78) * mm, "radius": 0.62 * mm});
            skCircle(sketch, "E10.0.28.12", {"center": v(21.93, -29.03) * mm, "radius": 0.62 * mm});
            skCircle(sketch, "E10.0.28.13", {"center": v(21.93, -32.28) * mm, "radius": 0.62 * mm});
            skCircle(sketch, "E10.0.28.14", {"center": v(21.93, -35.53) * mm, "radius": 0.62 * mm});
            skCircle(sketch, "E10.0.29.6", {"center": v(25.18, -9.53) * mm, "radius": 0.62 * mm});
            skCircle(sketch, "E10.0.29.7", {"center": v(25.18, -12.78) * mm, "radius": 0.62 * mm});
            skCircle(sketch, "E10.0.29.8", {"center": v(25.18, -16.03) * mm, "radius": 0.62 * mm});
            skCircle(sketch, "E10.0.29.9", {"center": v(25.18, -19.28) * mm, "radius": 0.62 * mm});
            skCircle(sketch, "E10.0.29.10", {"center": v(25.18, -22.53) * mm, "radius": 0.62 * mm});
            skCircle(sketch, "E10.0.29.11", {"center": v(25.18, -25.78) * mm, "radius": 0.62 * mm});
            skCircle(sketch, "E10.0.29.12", {"center": v(25.18, -29.03) * mm, "radius": 0.62 * mm});
            skCircle(sketch, "E10.0.29.13", {"center": v(25.18, -32.28) * mm, "radius": 0.62 * mm});
            skCircle(sketch, "E10.0.29.14", {"center": v(25.18, -35.53) * mm, "radius": 0.62 * mm});
            skCircle(sketch, "E10.0.30.6", {"center": v(28.43, -9.53) * mm, "radius": 0.62 * mm});
            skCircle(sketch, "E10.0.30.7", {"center": v(28.43, -12.78) * mm, "radius": 0.62 * mm});
            skCircle(sketch, "E10.0.30.8", {"center": v(28.43, -16.03) * mm, "radius": 0.62 * mm});
            skCircle(sketch, "E10.0.30.9", {"center": v(28.43, -19.28) * mm, "radius": 0.62 * mm});
            skCircle(sketch, "E10.0.30.10", {"center": v(28.43, -22.53) * mm, "radius": 0.62 * mm});
            skCircle(sketch, "E10.0.30.11", {"center": v(28.43, -25.78) * mm, "radius": 0.62 * mm});
            skCircle(sketch, "E10.0.30.12", {"center": v(28.43, -29.03) * mm, "radius": 0.62 * mm});
            skCircle(sketch, "E10.0.30.13", {"center": v(28.43, -32.28) * mm, "radius": 0.62 * mm});
            skCircle(sketch, "E10.0.30.14", {"center": v(28.43, -35.53) * mm, "radius": 0.62 * mm});
            skCircle(sketch, "E10.0.31.6", {"center": v(31.68, -9.53) * mm, "radius": 0.62 * mm});
            skCircle(sketch, "E10.0.31.7", {"center": v(31.68, -12.78) * mm, "radius": 0.62 * mm});
            skCircle(sketch, "E10.0.31.8", {"center": v(31.68, -16.03) * mm, "radius": 0.62 * mm});
            skCircle(sketch, "E10.0.31.9", {"center": v(31.68, -19.28) * mm, "radius": 0.62 * mm});
            skCircle(sketch, "E10.0.31.10", {"center": v(31.68, -22.53) * mm, "radius": 0.62 * mm});
            skCircle(sketch, "E10.0.31.11", {"center": v(31.68, -25.78) * mm, "radius": 0.62 * mm});
            skCircle(sketch, "E10.0.31.12", {"center": v(31.68, -29.03) * mm, "radius": 0.62 * mm});
            skCircle(sketch, "E10.0.31.13", {"center": v(31.68, -32.28) * mm, "radius": 0.62 * mm});
            skCircle(sketch, "E10.0.31.14", {"center": v(31.68, -35.53) * mm, "radius": 0.62 * mm});
            skCircle(sketch, "E10.0.32.6", {"center": v(34.93, -9.53) * mm, "radius": 0.62 * mm});
            skCircle(sketch, "E10.0.32.7", {"center": v(34.93, -12.78) * mm, "radius": 0.62 * mm});
            skCircle(sketch, "E10.0.32.8", {"center": v(34.93, -16.03) * mm, "radius": 0.62 * mm});
            skCircle(sketch, "E10.0.32.9", {"center": v(34.93, -19.28) * mm, "radius": 0.62 * mm});
            skCircle(sketch, "E10.0.32.10", {"center": v(34.93, -22.53) * mm, "radius": 0.62 * mm});
            skCircle(sketch, "E10.0.32.11", {"center": v(34.93, -25.78) * mm, "radius": 0.62 * mm});
            skCircle(sketch, "E10.0.32.12", {"center": v(34.93, -29.03) * mm, "radius": 0.62 * mm});
            skCircle(sketch, "E10.0.32.13", {"center": v(34.93, -32.28) * mm, "radius": 0.62 * mm});
            skCircle(sketch, "E10.0.32.14", {"center": v(34.93, -35.53) * mm, "radius": 0.62 * mm});
            skCircle(sketch, "E10.0.33.6", {"center": v(38.18, -9.53) * mm, "radius": 0.62 * mm});
            skCircle(sketch, "E10.0.33.7", {"center": v(38.18, -12.78) * mm, "radius": 0.62 * mm});
            skCircle(sketch, "E10.0.33.8", {"center": v(38.18, -16.03) * mm, "radius": 0.62 * mm});
            skCircle(sketch, "E10.0.33.9", {"center": v(38.18, -19.28) * mm, "radius": 0.62 * mm});
            skCircle(sketch, "E10.0.33.10", {"center": v(38.18, -22.53) * mm, "radius": 0.62 * mm});
            skCircle(sketch, "E10.0.33.11", {"center": v(38.18, -25.78) * mm, "radius": 0.62 * mm});
            skCircle(sketch, "E10.0.33.12", {"center": v(38.18, -29.03) * mm, "radius": 0.62 * mm});
            skCircle(sketch, "E10.0.33.13", {"center": v(38.18, -32.28) * mm, "radius": 0.62 * mm});
            skCircle(sketch, "E10.0.33.14", {"center": v(38.18, -35.53) * mm, "radius": 0.62 * mm});
            skCircle(sketch, "E10.0.34.6", {"center": v(41.43, -9.53) * mm, "radius": 0.62 * mm});
            skCircle(sketch, "E10.0.34.7", {"center": v(41.43, -12.78) * mm, "radius": 0.62 * mm});
            skCircle(sketch, "E10.0.34.8", {"center": v(41.43, -16.03) * mm, "radius": 0.62 * mm});
            skCircle(sketch, "E10.0.34.9", {"center": v(41.43, -19.28) * mm, "radius": 0.62 * mm});
            skCircle(sketch, "E10.0.34.10", {"center": v(41.43, -22.53) * mm, "radius": 0.62 * mm});
            skCircle(sketch, "E10.0.34.11", {"center": v(41.43, -25.78) * mm, "radius": 0.62 * mm});
            skCircle(sketch, "E10.0.34.12", {"center": v(41.43, -29.03) * mm, "radius": 0.62 * mm});
            skCircle(sketch, "E10.0.34.13", {"center": v(41.43, -32.28) * mm, "radius": 0.62 * mm});
            skCircle(sketch, "E10.0.34.14", {"center": v(41.43, -35.53) * mm, "radius": 0.62 * mm});
            skCircle(sketch, "E10.0.35.6", {"center": v(44.68, -9.53) * mm, "radius": 0.62 * mm});
            skCircle(sketch, "E10.0.35.7", {"center": v(44.68, -12.78) * mm, "radius": 0.62 * mm});
            skCircle(sketch, "E10.0.35.8", {"center": v(44.68, -16.03) * mm, "radius": 0.62 * mm});
            skCircle(sketch, "E10.0.35.9", {"center": v(44.68, -19.28) * mm, "radius": 0.62 * mm});
            skCircle(sketch, "E10.0.35.10", {"center": v(44.68, -22.53) * mm, "radius": 0.62 * mm});
            skCircle(sketch, "E10.0.35.11", {"center": v(44.68, -25.78) * mm, "radius": 0.62 * mm});
            skCircle(sketch, "E10.0.35.12", {"center": v(44.68, -29.03) * mm, "radius": 0.62 * mm});
            skCircle(sketch, "E10.0.35.13", {"center": v(44.68, -32.28) * mm, "radius": 0.62 * mm});
            skCircle(sketch, "E10.0.35.14", {"center": v(44.68, -35.53) * mm, "radius": 0.62 * mm});
            skCircle(sketch, "E10.0.36.6", {"center": v(47.93, -9.53) * mm, "radius": 0.62 * mm});
            skCircle(sketch, "E10.0.36.7", {"center": v(47.93, -12.78) * mm, "radius": 0.62 * mm});
            skCircle(sketch, "E10.0.36.8", {"center": v(47.93, -16.03) * mm, "radius": 0.62 * mm});
            skCircle(sketch, "E10.0.36.9", {"center": v(47.93, -19.28) * mm, "radius": 0.62 * mm});
            skCircle(sketch, "E10.0.36.10", {"center": v(47.93, -22.53) * mm, "radius": 0.62 * mm});
            skCircle(sketch, "E10.0.36.11", {"center": v(47.93, -25.78) * mm, "radius": 0.62 * mm});
            skCircle(sketch, "E10.0.36.12", {"center": v(47.93, -29.03) * mm, "radius": 0.62 * mm});
            skCircle(sketch, "E10.0.36.13", {"center": v(47.93, -32.28) * mm, "radius": 0.62 * mm});
            skCircle(sketch, "E10.0.36.14", {"center": v(47.93, -35.53) * mm, "radius": 0.62 * mm});
            skCircle(sketch, "E10.0.37.6", {"center": v(51.18, -9.53) * mm, "radius": 0.62 * mm});
            skCircle(sketch, "E10.0.37.7", {"center": v(51.18, -12.78) * mm, "radius": 0.62 * mm});
            skCircle(sketch, "E10.0.37.8", {"center": v(51.18, -16.03) * mm, "radius": 0.62 * mm});
            skCircle(sketch, "E10.0.37.9", {"center": v(51.18, -19.28) * mm, "radius": 0.62 * mm});
            skCircle(sketch, "E10.0.37.10", {"center": v(51.18, -22.53) * mm, "radius": 0.62 * mm});
            skCircle(sketch, "E10.0.37.11", {"center": v(51.18, -25.78) * mm, "radius": 0.62 * mm});
            skCircle(sketch, "E10.0.37.12", {"center": v(51.18, -29.03) * mm, "radius": 0.62 * mm});
            skCircle(sketch, "E10.0.37.13", {"center": v(51.18, -32.28) * mm, "radius": 0.62 * mm});
            skCircle(sketch, "E10.0.37.14", {"center": v(51.18, -35.53) * mm, "radius": 0.62 * mm});
            skCircle(sketch, "E10.0.38.6", {"center": v(54.43, -9.53) * mm, "radius": 0.62 * mm});
            skCircle(sketch, "E10.0.38.7", {"center": v(54.43, -12.78) * mm, "radius": 0.62 * mm});
            skCircle(sketch, "E10.0.38.8", {"center": v(54.43, -16.03) * mm, "radius": 0.62 * mm});
            skCircle(sketch, "E10.0.38.9", {"center": v(54.43, -19.28) * mm, "radius": 0.62 * mm});
            skCircle(sketch, "E10.0.38.10", {"center": v(54.43, -22.53) * mm, "radius": 0.62 * mm});
            skCircle(sketch, "E10.0.38.11", {"center": v(54.43, -25.78) * mm, "radius": 0.62 * mm});
            skCircle(sketch, "E10.0.38.12", {"center": v(54.43, -29.03) * mm, "radius": 0.62 * mm});
            skCircle(sketch, "E10.0.38.13", {"center": v(54.43, -32.28) * mm, "radius": 0.62 * mm});
            skCircle(sketch, "E10.0.38.14", {"center": v(54.43, -35.53) * mm, "radius": 0.62 * mm});
            skCircle(sketch, "E10.0.39.6", {"center": v(57.68, -9.53) * mm, "radius": 0.62 * mm});
            skCircle(sketch, "E10.0.39.7", {"center": v(57.68, -12.78) * mm, "radius": 0.62 * mm});
            skCircle(sketch, "E10.0.39.8", {"center": v(57.68, -16.03) * mm, "radius": 0.62 * mm});
            skCircle(sketch, "E10.0.39.9", {"center": v(57.68, -19.28) * mm, "radius": 0.62 * mm});
            skCircle(sketch, "E10.0.39.10", {"center": v(57.68, -22.53) * mm, "radius": 0.62 * mm});
            skCircle(sketch, "E10.0.39.11", {"center": v(57.68, -25.78) * mm, "radius": 0.62 * mm});
            skCircle(sketch, "E10.0.39.12", {"center": v(57.68, -29.03) * mm, "radius": 0.62 * mm});
            skCircle(sketch, "E10.0.39.13", {"center": v(57.68, -32.28) * mm, "radius": 0.62 * mm});
            skCircle(sketch, "E10.0.39.14", {"center": v(57.68, -35.53) * mm, "radius": 0.62 * mm});
            skCircle(sketch, "E10.0.40.6", {"center": v(60.93, -9.53) * mm, "radius": 0.62 * mm});
            skCircle(sketch, "E10.0.40.7", {"center": v(60.93, -12.78) * mm, "radius": 0.62 * mm});
            skCircle(sketch, "E10.0.40.8", {"center": v(60.93, -16.03) * mm, "radius": 0.62 * mm});
            skCircle(sketch, "E10.0.40.9", {"center": v(60.93, -19.28) * mm, "radius": 0.62 * mm});
            skCircle(sketch, "E10.0.40.10", {"center": v(60.93, -22.53) * mm, "radius": 0.62 * mm});
            skCircle(sketch, "E10.0.40.11", {"center": v(60.93, -25.78) * mm, "radius": 0.62 * mm});
            skCircle(sketch, "E10.0.40.12", {"center": v(60.93, -29.03) * mm, "radius": 0.62 * mm});
            skCircle(sketch, "E10.0.40.13", {"center": v(60.93, -32.28) * mm, "radius": 0.62 * mm});
            skCircle(sketch, "E10.0.40.14", {"center": v(60.93, -35.53) * mm, "radius": 0.62 * mm});
            skCircle(sketch, "E10.0.41.6", {"center": v(64.18, -9.53) * mm, "radius": 0.62 * mm});
            skCircle(sketch, "E10.0.41.7", {"center": v(64.18, -12.78) * mm, "radius": 0.62 * mm});
            skCircle(sketch, "E10.0.41.8", {"center": v(64.18, -16.03) * mm, "radius": 0.62 * mm});
            skCircle(sketch, "E10.0.41.9", {"center": v(64.18, -19.28) * mm, "radius": 0.62 * mm});
            skCircle(sketch, "E10.0.41.10", {"center": v(64.18, -22.53) * mm, "radius": 0.62 * mm});
            skCircle(sketch, "E10.0.41.11", {"center": v(64.18, -25.78) * mm, "radius": 0.62 * mm});
            skCircle(sketch, "E10.0.41.12", {"center": v(64.18, -29.03) * mm, "radius": 0.62 * mm});
            skCircle(sketch, "E10.0.41.13", {"center": v(64.18, -32.28) * mm, "radius": 0.62 * mm});
            skCircle(sketch, "E10.0.41.14", {"center": v(64.18, -35.53) * mm, "radius": 0.62 * mm});
            skCircle(sketch, "E10.0.42.6", {"center": v(67.43, -9.53) * mm, "radius": 0.62 * mm});
            skCircle(sketch, "E10.0.42.7", {"center": v(67.43, -12.78) * mm, "radius": 0.62 * mm});
            skCircle(sketch, "E10.0.42.8", {"center": v(67.43, -16.03) * mm, "radius": 0.62 * mm});
            skCircle(sketch, "E10.0.42.9", {"center": v(67.43, -19.28) * mm, "radius": 0.62 * mm});
            skCircle(sketch, "E10.0.42.10", {"center": v(67.43, -22.53) * mm, "radius": 0.62 * mm});
            skCircle(sketch, "E10.0.42.11", {"center": v(67.43, -25.78) * mm, "radius": 0.62 * mm});
            skCircle(sketch, "E10.0.42.12", {"center": v(67.43, -29.03) * mm, "radius": 0.62 * mm});
            skCircle(sketch, "E10.0.42.13", {"center": v(67.43, -32.28) * mm, "radius": 0.62 * mm});
            skCircle(sketch, "E10.0.42.14", {"center": v(67.43, -35.53) * mm, "radius": 0.62 * mm});
            skCircle(sketch, "E10.0.43.6", {"center": v(70.68, -9.53) * mm, "radius": 0.62 * mm});
            skCircle(sketch, "E10.0.43.7", {"center": v(70.68, -12.78) * mm, "radius": 0.62 * mm});
            skCircle(sketch, "E10.0.43.8", {"center": v(70.68, -16.03) * mm, "radius": 0.62 * mm});
            skCircle(sketch, "E10.0.43.9", {"center": v(70.68, -19.28) * mm, "radius": 0.62 * mm});
            skCircle(sketch, "E10.0.43.10", {"center": v(70.68, -22.53) * mm, "radius": 0.62 * mm});
            skCircle(sketch, "E10.0.43.11", {"center": v(70.68, -25.78) * mm, "radius": 0.62 * mm});
            skCircle(sketch, "E10.0.43.12", {"center": v(70.68, -29.03) * mm, "radius": 0.62 * mm});
            skCircle(sketch, "E10.0.43.13", {"center": v(70.68, -32.28) * mm, "radius": 0.62 * mm});
            skCircle(sketch, "E10.0.43.14", {"center": v(70.68, -35.53) * mm, "radius": 0.62 * mm});
            skCircle(sketch, "E10.0.44.6", {"center": v(73.93, -9.53) * mm, "radius": 0.62 * mm});
            skCircle(sketch, "E10.0.44.7", {"center": v(73.93, -12.78) * mm, "radius": 0.62 * mm});
            skCircle(sketch, "E10.0.44.8", {"center": v(73.93, -16.03) * mm, "radius": 0.62 * mm});
            skCircle(sketch, "E10.0.44.9", {"center": v(73.93, -19.28) * mm, "radius": 0.62 * mm});
            skCircle(sketch, "E10.0.44.10", {"center": v(73.93, -22.53) * mm, "radius": 0.62 * mm});
            skCircle(sketch, "E10.0.44.11", {"center": v(73.93, -25.78) * mm, "radius": 0.62 * mm});
            skCircle(sketch, "E10.0.44.12", {"center": v(73.93, -29.03) * mm, "radius": 0.62 * mm});
            skCircle(sketch, "E10.0.44.13", {"center": v(73.93, -32.28) * mm, "radius": 0.62 * mm});
            skCircle(sketch, "E10.0.44.14", {"center": v(73.93, -35.53) * mm, "radius": 0.62 * mm});
            skCircle(sketch, "E11.0.0.6", {"center": v(-67.45, -11.16) * mm, "radius": 0.62 * mm});
            skCircle(sketch, "E11.0.0.7", {"center": v(-67.45, -14.4) * mm, "radius": 0.62 * mm});
            skCircle(sketch, "E11.0.0.8", {"center": v(-67.45, -17.66) * mm, "radius": 0.62 * mm});
            skCircle(sketch, "E11.0.0.9", {"center": v(-67.45, -20.9) * mm, "radius": 0.62 * mm});
            skCircle(sketch, "E11.0.0.10", {"center": v(-67.45, -24.16) * mm, "radius": 0.62 * mm});
            skCircle(sketch, "E11.0.0.11", {"center": v(-67.45, -27.4) * mm, "radius": 0.62 * mm});
            skCircle(sketch, "E11.0.0.12", {"center": v(-67.45, -30.66) * mm, "radius": 0.62 * mm});
            skCircle(sketch, "E11.0.0.13", {"center": v(-67.45, -33.9) * mm, "radius": 0.62 * mm});
            skCircle(sketch, "E11.0.0.14", {"center": v(-67.45, -37.16) * mm, "radius": 0.62 * mm});
            skCircle(sketch, "E11.0.0.15", {"center": v(-67.45, -40.4) * mm, "radius": 0.62 * mm});
            skCircle(sketch, "E11.0.1.6", {"center": v(-64.2, -11.16) * mm, "radius": 0.62 * mm});
            skCircle(sketch, "E11.0.1.7", {"center": v(-64.2, -14.4) * mm, "radius": 0.62 * mm});
            skCircle(sketch, "E11.0.1.8", {"center": v(-64.2, -17.66) * mm, "radius": 0.62 * mm});
            skCircle(sketch, "E11.0.1.9", {"center": v(-64.2, -20.9) * mm, "radius": 0.62 * mm});
            skCircle(sketch, "E11.0.1.10", {"center": v(-64.2, -24.16) * mm, "radius": 0.62 * mm});
            skCircle(sketch, "E11.0.1.11", {"center": v(-64.2, -27.4) * mm, "radius": 0.62 * mm});
            skCircle(sketch, "E11.0.1.12", {"center": v(-64.2, -30.66) * mm, "radius": 0.62 * mm});
            skCircle(sketch, "E11.0.1.13", {"center": v(-64.2, -33.9) * mm, "radius": 0.62 * mm});
            skCircle(sketch, "E11.0.1.14", {"center": v(-64.2, -37.16) * mm, "radius": 0.62 * mm});
            skCircle(sketch, "E11.0.1.15", {"center": v(-64.2, -40.4) * mm, "radius": 0.62 * mm});
            skCircle(sketch, "E11.0.2.6", {"center": v(-60.95, -11.16) * mm, "radius": 0.62 * mm});
            skCircle(sketch, "E11.0.2.7", {"center": v(-60.95, -14.4) * mm, "radius": 0.62 * mm});
            skCircle(sketch, "E11.0.2.8", {"center": v(-60.95, -17.66) * mm, "radius": 0.62 * mm});
            skCircle(sketch, "E11.0.2.9", {"center": v(-60.95, -20.9) * mm, "radius": 0.62 * mm});
            skCircle(sketch, "E11.0.2.10", {"center": v(-60.95, -24.16) * mm, "radius": 0.62 * mm});
            skCircle(sketch, "E11.0.2.11", {"center": v(-60.95, -27.4) * mm, "radius": 0.62 * mm});
            skCircle(sketch, "E11.0.2.12", {"center": v(-60.95, -30.66) * mm, "radius": 0.62 * mm});
            skCircle(sketch, "E11.0.2.13", {"center": v(-60.95, -33.9) * mm, "radius": 0.62 * mm});
            skCircle(sketch, "E11.0.2.14", {"center": v(-60.95, -37.16) * mm, "radius": 0.62 * mm});
            skCircle(sketch, "E11.0.2.15", {"center": v(-60.95, -40.4) * mm, "radius": 0.62 * mm});
            skCircle(sketch, "E11.0.3.6", {"center": v(-57.7, -11.16) * mm, "radius": 0.62 * mm});
            skCircle(sketch, "E11.0.3.7", {"center": v(-57.7, -14.4) * mm, "radius": 0.62 * mm});
            skCircle(sketch, "E11.0.3.8", {"center": v(-57.7, -17.66) * mm, "radius": 0.62 * mm});
            skCircle(sketch, "E11.0.3.9", {"center": v(-57.7, -20.9) * mm, "radius": 0.62 * mm});
            skCircle(sketch, "E11.0.3.10", {"center": v(-57.7, -24.16) * mm, "radius": 0.62 * mm});
            skCircle(sketch, "E11.0.3.11", {"center": v(-57.7, -27.4) * mm, "radius": 0.62 * mm});
            skCircle(sketch, "E11.0.3.12", {"center": v(-57.7, -30.66) * mm, "radius": 0.62 * mm});
            skCircle(sketch, "E11.0.3.13", {"center": v(-57.7, -33.9) * mm, "radius": 0.62 * mm});
            skCircle(sketch, "E11.0.3.14", {"center": v(-57.7, -37.16) * mm, "radius": 0.62 * mm});
            skCircle(sketch, "E11.0.3.15", {"center": v(-57.7, -40.4) * mm, "radius": 0.62 * mm});
            skCircle(sketch, "E11.0.4.6", {"center": v(-54.45, -11.16) * mm, "radius": 0.62 * mm});
            skCircle(sketch, "E11.0.4.7", {"center": v(-54.45, -14.4) * mm, "radius": 0.62 * mm});
            skCircle(sketch, "E11.0.4.8", {"center": v(-54.45, -17.66) * mm, "radius": 0.62 * mm});
            skCircle(sketch, "E11.0.4.9", {"center": v(-54.45, -20.9) * mm, "radius": 0.62 * mm});
            skCircle(sketch, "E11.0.4.10", {"center": v(-54.45, -24.16) * mm, "radius": 0.62 * mm});
            skCircle(sketch, "E11.0.4.11", {"center": v(-54.45, -27.4) * mm, "radius": 0.62 * mm});
            skCircle(sketch, "E11.0.4.12", {"center": v(-54.45, -30.66) * mm, "radius": 0.62 * mm});
            skCircle(sketch, "E11.0.4.13", {"center": v(-54.45, -33.9) * mm, "radius": 0.62 * mm});
            skCircle(sketch, "E11.0.4.14", {"center": v(-54.45, -37.16) * mm, "radius": 0.62 * mm});
            skCircle(sketch, "E11.0.4.15", {"center": v(-54.45, -40.4) * mm, "radius": 0.62 * mm});
            skCircle(sketch, "E11.0.5.6", {"center": v(-51.2, -11.16) * mm, "radius": 0.62 * mm});
            skCircle(sketch, "E11.0.5.7", {"center": v(-51.2, -14.4) * mm, "radius": 0.62 * mm});
            skCircle(sketch, "E11.0.5.8", {"center": v(-51.2, -17.66) * mm, "radius": 0.62 * mm});
            skCircle(sketch, "E11.0.5.9", {"center": v(-51.2, -20.9) * mm, "radius": 0.62 * mm});
            skCircle(sketch, "E11.0.5.10", {"center": v(-51.2, -24.16) * mm, "radius": 0.62 * mm});
            skCircle(sketch, "E11.0.5.11", {"center": v(-51.2, -27.4) * mm, "radius": 0.62 * mm});
            skCircle(sketch, "E11.0.5.12", {"center": v(-51.2, -30.66) * mm, "radius": 0.62 * mm});
            skCircle(sketch, "E11.0.5.13", {"center": v(-51.2, -33.9) * mm, "radius": 0.62 * mm});
            skCircle(sketch, "E11.0.5.14", {"center": v(-51.2, -37.16) * mm, "radius": 0.62 * mm});
            skCircle(sketch, "E11.0.5.15", {"center": v(-51.2, -40.4) * mm, "radius": 0.62 * mm});
            skCircle(sketch, "E11.0.6.6", {"center": v(-47.95, -11.16) * mm, "radius": 0.62 * mm});
            skCircle(sketch, "E11.0.6.7", {"center": v(-47.95, -14.4) * mm, "radius": 0.62 * mm});
            skCircle(sketch, "E11.0.6.8", {"center": v(-47.95, -17.66) * mm, "radius": 0.62 * mm});
            skCircle(sketch, "E11.0.6.9", {"center": v(-47.95, -20.9) * mm, "radius": 0.62 * mm});
            skCircle(sketch, "E11.0.6.10", {"center": v(-47.95, -24.16) * mm, "radius": 0.62 * mm});
            skCircle(sketch, "E11.0.6.11", {"center": v(-47.95, -27.4) * mm, "radius": 0.62 * mm});
            skCircle(sketch, "E11.0.6.12", {"center": v(-47.95, -30.66) * mm, "radius": 0.62 * mm});
            skCircle(sketch, "E11.0.6.13", {"center": v(-47.95, -33.9) * mm, "radius": 0.62 * mm});
            skCircle(sketch, "E11.0.6.14", {"center": v(-47.95, -37.16) * mm, "radius": 0.62 * mm});
            skCircle(sketch, "E11.0.6.15", {"center": v(-47.95, -40.4) * mm, "radius": 0.62 * mm});
            skCircle(sketch, "E11.0.7.6", {"center": v(-44.7, -11.16) * mm, "radius": 0.62 * mm});
            skCircle(sketch, "E11.0.7.7", {"center": v(-44.7, -14.4) * mm, "radius": 0.62 * mm});
            skCircle(sketch, "E11.0.7.8", {"center": v(-44.7, -17.66) * mm, "radius": 0.62 * mm});
            skCircle(sketch, "E11.0.7.9", {"center": v(-44.7, -20.9) * mm, "radius": 0.62 * mm});
            skCircle(sketch, "E11.0.7.10", {"center": v(-44.7, -24.16) * mm, "radius": 0.62 * mm});
            skCircle(sketch, "E11.0.7.11", {"center": v(-44.7, -27.4) * mm, "radius": 0.62 * mm});
            skCircle(sketch, "E11.0.7.12", {"center": v(-44.7, -30.66) * mm, "radius": 0.62 * mm});
            skCircle(sketch, "E11.0.7.13", {"center": v(-44.7, -33.9) * mm, "radius": 0.62 * mm});
            skCircle(sketch, "E11.0.7.14", {"center": v(-44.7, -37.16) * mm, "radius": 0.62 * mm});
            skCircle(sketch, "E11.0.7.15", {"center": v(-44.7, -40.4) * mm, "radius": 0.62 * mm});
            skCircle(sketch, "E11.0.8.6", {"center": v(-41.45, -11.16) * mm, "radius": 0.62 * mm});
            skCircle(sketch, "E11.0.8.7", {"center": v(-41.45, -14.4) * mm, "radius": 0.62 * mm});
            skCircle(sketch, "E11.0.8.8", {"center": v(-41.45, -17.66) * mm, "radius": 0.62 * mm});
            skCircle(sketch, "E11.0.8.9", {"center": v(-41.45, -20.9) * mm, "radius": 0.62 * mm});
            skCircle(sketch, "E11.0.8.10", {"center": v(-41.45, -24.16) * mm, "radius": 0.62 * mm});
            skCircle(sketch, "E11.0.8.11", {"center": v(-41.45, -27.4) * mm, "radius": 0.62 * mm});
            skCircle(sketch, "E11.0.8.12", {"center": v(-41.45, -30.66) * mm, "radius": 0.62 * mm});
            skCircle(sketch, "E11.0.8.13", {"center": v(-41.45, -33.9) * mm, "radius": 0.62 * mm});
            skCircle(sketch, "E11.0.8.14", {"center": v(-41.45, -37.16) * mm, "radius": 0.62 * mm});
            skCircle(sketch, "E11.0.8.15", {"center": v(-41.45, -40.4) * mm, "radius": 0.62 * mm});
            skCircle(sketch, "E11.0.9.6", {"center": v(-38.2, -11.16) * mm, "radius": 0.62 * mm});
            skCircle(sketch, "E11.0.9.7", {"center": v(-38.2, -14.4) * mm, "radius": 0.62 * mm});
            skCircle(sketch, "E11.0.9.8", {"center": v(-38.2, -17.66) * mm, "radius": 0.62 * mm});
            skCircle(sketch, "E11.0.9.9", {"center": v(-38.2, -20.9) * mm, "radius": 0.62 * mm});
            skCircle(sketch, "E11.0.9.10", {"center": v(-38.2, -24.16) * mm, "radius": 0.62 * mm});
            skCircle(sketch, "E11.0.9.11", {"center": v(-38.2, -27.4) * mm, "radius": 0.62 * mm});
            skCircle(sketch, "E11.0.9.12", {"center": v(-38.2, -30.66) * mm, "radius": 0.62 * mm});
            skCircle(sketch, "E11.0.9.13", {"center": v(-38.2, -33.9) * mm, "radius": 0.62 * mm});
            skCircle(sketch, "E11.0.9.14", {"center": v(-38.2, -37.16) * mm, "radius": 0.62 * mm});
            skCircle(sketch, "E11.0.9.15", {"center": v(-38.2, -40.4) * mm, "radius": 0.62 * mm});
            skCircle(sketch, "E11.0.10.6", {"center": v(-34.95, -11.16) * mm, "radius": 0.62 * mm});
            skCircle(sketch, "E11.0.10.7", {"center": v(-34.95, -14.4) * mm, "radius": 0.62 * mm});
            skCircle(sketch, "E11.0.10.8", {"center": v(-34.95, -17.66) * mm, "radius": 0.62 * mm});
            skCircle(sketch, "E11.0.10.9", {"center": v(-34.95, -20.9) * mm, "radius": 0.62 * mm});
            skCircle(sketch, "E11.0.10.10", {"center": v(-34.95, -24.16) * mm, "radius": 0.62 * mm});
            skCircle(sketch, "E11.0.10.11", {"center": v(-34.95, -27.4) * mm, "radius": 0.62 * mm});
            skCircle(sketch, "E11.0.10.12", {"center": v(-34.95, -30.66) * mm, "radius": 0.62 * mm});
            skCircle(sketch, "E11.0.10.13", {"center": v(-34.95, -33.9) * mm, "radius": 0.62 * mm});
            skCircle(sketch, "E11.0.10.14", {"center": v(-34.95, -37.16) * mm, "radius": 0.62 * mm});
            skCircle(sketch, "E11.0.10.15", {"center": v(-34.95, -40.4) * mm, "radius": 0.62 * mm});
            skCircle(sketch, "E11.0.11.6", {"center": v(-31.7, -11.16) * mm, "radius": 0.62 * mm});
            skCircle(sketch, "E11.0.11.7", {"center": v(-31.7, -14.4) * mm, "radius": 0.62 * mm});
            skCircle(sketch, "E11.0.11.8", {"center": v(-31.7, -17.66) * mm, "radius": 0.62 * mm});
            skCircle(sketch, "E11.0.11.9", {"center": v(-31.7, -20.9) * mm, "radius": 0.62 * mm});
            skCircle(sketch, "E11.0.11.10", {"center": v(-31.7, -24.16) * mm, "radius": 0.62 * mm});
            skCircle(sketch, "E11.0.11.11", {"center": v(-31.7, -27.4) * mm, "radius": 0.62 * mm});
            skCircle(sketch, "E11.0.11.12", {"center": v(-31.7, -30.66) * mm, "radius": 0.62 * mm});
            skCircle(sketch, "E11.0.11.13", {"center": v(-31.7, -33.9) * mm, "radius": 0.62 * mm});
            skCircle(sketch, "E11.0.11.14", {"center": v(-31.7, -37.16) * mm, "radius": 0.62 * mm});
            skCircle(sketch, "E11.0.11.15", {"center": v(-31.7, -40.4) * mm, "radius": 0.62 * mm});
            skCircle(sketch, "E11.0.12.6", {"center": v(-28.45, -11.16) * mm, "radius": 0.62 * mm});
            skCircle(sketch, "E11.0.12.7", {"center": v(-28.45, -14.4) * mm, "radius": 0.62 * mm});
            skCircle(sketch, "E11.0.12.8", {"center": v(-28.45, -17.66) * mm, "radius": 0.62 * mm});
            skCircle(sketch, "E11.0.12.9", {"center": v(-28.45, -20.9) * mm, "radius": 0.62 * mm});
            skCircle(sketch, "E11.0.12.10", {"center": v(-28.45, -24.16) * mm, "radius": 0.62 * mm});
            skCircle(sketch, "E11.0.12.11", {"center": v(-28.45, -27.4) * mm, "radius": 0.62 * mm});
            skCircle(sketch, "E11.0.12.12", {"center": v(-28.45, -30.66) * mm, "radius": 0.62 * mm});
            skCircle(sketch, "E11.0.12.13", {"center": v(-28.45, -33.9) * mm, "radius": 0.62 * mm});
            skCircle(sketch, "E11.0.12.14", {"center": v(-28.45, -37.16) * mm, "radius": 0.62 * mm});
            skCircle(sketch, "E11.0.12.15", {"center": v(-28.45, -40.4) * mm, "radius": 0.62 * mm});
            skCircle(sketch, "E11.0.13.6", {"center": v(-25.2, -11.16) * mm, "radius": 0.62 * mm});
            skCircle(sketch, "E11.0.13.7", {"center": v(-25.2, -14.4) * mm, "radius": 0.62 * mm});
            skCircle(sketch, "E11.0.13.8", {"center": v(-25.2, -17.66) * mm, "radius": 0.62 * mm});
            skCircle(sketch, "E11.0.13.9", {"center": v(-25.2, -20.9) * mm, "radius": 0.62 * mm});
            skCircle(sketch, "E11.0.13.10", {"center": v(-25.2, -24.16) * mm, "radius": 0.62 * mm});
            skCircle(sketch, "E11.0.13.11", {"center": v(-25.2, -27.4) * mm, "radius": 0.62 * mm});
            skCircle(sketch, "E11.0.13.12", {"center": v(-25.2, -30.66) * mm, "radius": 0.62 * mm});
            skCircle(sketch, "E11.0.13.13", {"center": v(-25.2, -33.9) * mm, "radius": 0.62 * mm});
            skCircle(sketch, "E11.0.13.14", {"center": v(-25.2, -37.16) * mm, "radius": 0.62 * mm});
            skCircle(sketch, "E11.0.13.15", {"center": v(-25.2, -40.4) * mm, "radius": 0.62 * mm});
            skCircle(sketch, "E11.0.14.6", {"center": v(-21.95, -11.16) * mm, "radius": 0.62 * mm});
            skCircle(sketch, "E11.0.14.7", {"center": v(-21.95, -14.4) * mm, "radius": 0.62 * mm});
            skCircle(sketch, "E11.0.14.8", {"center": v(-21.95, -17.66) * mm, "radius": 0.62 * mm});
            skCircle(sketch, "E11.0.14.9", {"center": v(-21.95, -20.9) * mm, "radius": 0.62 * mm});
            skCircle(sketch, "E11.0.14.10", {"center": v(-21.95, -24.16) * mm, "radius": 0.62 * mm});
            skCircle(sketch, "E11.0.14.11", {"center": v(-21.95, -27.4) * mm, "radius": 0.62 * mm});
            skCircle(sketch, "E11.0.14.12", {"center": v(-21.95, -30.66) * mm, "radius": 0.62 * mm});
            skCircle(sketch, "E11.0.14.13", {"center": v(-21.95, -33.9) * mm, "radius": 0.62 * mm});
            skCircle(sketch, "E11.0.14.14", {"center": v(-21.95, -37.16) * mm, "radius": 0.62 * mm});
            skCircle(sketch, "E11.0.14.15", {"center": v(-21.95, -40.4) * mm, "radius": 0.62 * mm});
            skCircle(sketch, "E11.0.15.6", {"center": v(-18.7, -11.16) * mm, "radius": 0.62 * mm});
            skCircle(sketch, "E11.0.15.7", {"center": v(-18.7, -14.4) * mm, "radius": 0.62 * mm});
            skCircle(sketch, "E11.0.15.8", {"center": v(-18.7, -17.66) * mm, "radius": 0.62 * mm});
            skCircle(sketch, "E11.0.15.9", {"center": v(-18.7, -20.9) * mm, "radius": 0.62 * mm});
            skCircle(sketch, "E11.0.15.10", {"center": v(-18.7, -24.16) * mm, "radius": 0.62 * mm});
            skCircle(sketch, "E11.0.15.11", {"center": v(-18.7, -27.4) * mm, "radius": 0.62 * mm});
            skCircle(sketch, "E11.0.15.12", {"center": v(-18.7, -30.66) * mm, "radius": 0.62 * mm});
            skCircle(sketch, "E11.0.15.13", {"center": v(-18.7, -33.9) * mm, "radius": 0.62 * mm});
            skCircle(sketch, "E11.0.15.14", {"center": v(-18.7, -37.16) * mm, "radius": 0.62 * mm});
            skCircle(sketch, "E11.0.15.15", {"center": v(-18.7, -40.4) * mm, "radius": 0.62 * mm});
            skCircle(sketch, "E11.0.16.6", {"center": v(-15.45, -11.16) * mm, "radius": 0.62 * mm});
            skCircle(sketch, "E11.0.16.7", {"center": v(-15.45, -14.4) * mm, "radius": 0.62 * mm});
            skCircle(sketch, "E11.0.16.8", {"center": v(-15.45, -17.66) * mm, "radius": 0.62 * mm});
            skCircle(sketch, "E11.0.16.9", {"center": v(-15.45, -20.9) * mm, "radius": 0.62 * mm});
            skCircle(sketch, "E11.0.16.10", {"center": v(-15.45, -24.16) * mm, "radius": 0.62 * mm});
            skCircle(sketch, "E11.0.16.11", {"center": v(-15.45, -27.4) * mm, "radius": 0.62 * mm});
            skCircle(sketch, "E11.0.16.12", {"center": v(-15.45, -30.66) * mm, "radius": 0.62 * mm});
            skCircle(sketch, "E11.0.16.13", {"center": v(-15.45, -33.9) * mm, "radius": 0.62 * mm});
            skCircle(sketch, "E11.0.16.14", {"center": v(-15.45, -37.16) * mm, "radius": 0.62 * mm});
            skCircle(sketch, "E11.0.16.15", {"center": v(-15.45, -40.4) * mm, "radius": 0.62 * mm});
            skCircle(sketch, "E11.0.17.6", {"center": v(-12.2, -11.16) * mm, "radius": 0.62 * mm});
            skCircle(sketch, "E11.0.17.7", {"center": v(-12.2, -14.4) * mm, "radius": 0.62 * mm});
            skCircle(sketch, "E11.0.17.8", {"center": v(-12.2, -17.66) * mm, "radius": 0.62 * mm});
            skCircle(sketch, "E11.0.17.9", {"center": v(-12.2, -20.9) * mm, "radius": 0.62 * mm});
            skCircle(sketch, "E11.0.17.10", {"center": v(-12.2, -24.16) * mm, "radius": 0.62 * mm});
            skCircle(sketch, "E11.0.17.11", {"center": v(-12.2, -27.4) * mm, "radius": 0.62 * mm});
            skCircle(sketch, "E11.0.17.12", {"center": v(-12.2, -30.66) * mm, "radius": 0.62 * mm});
            skCircle(sketch, "E11.0.17.13", {"center": v(-12.2, -33.9) * mm, "radius": 0.62 * mm});
            skCircle(sketch, "E11.0.17.14", {"center": v(-12.2, -37.16) * mm, "radius": 0.62 * mm});
            skCircle(sketch, "E11.0.17.15", {"center": v(-12.2, -40.4) * mm, "radius": 0.62 * mm});
            skCircle(sketch, "E11.0.18.6", {"center": v(-8.95, -11.16) * mm, "radius": 0.62 * mm});
            skCircle(sketch, "E11.0.18.7", {"center": v(-8.95, -14.4) * mm, "radius": 0.62 * mm});
            skCircle(sketch, "E11.0.18.8", {"center": v(-8.95, -17.66) * mm, "radius": 0.62 * mm});
            skCircle(sketch, "E11.0.18.9", {"center": v(-8.95, -20.9) * mm, "radius": 0.62 * mm});
            skCircle(sketch, "E11.0.18.10", {"center": v(-8.95, -24.16) * mm, "radius": 0.62 * mm});
            skCircle(sketch, "E11.0.18.11", {"center": v(-8.95, -27.4) * mm, "radius": 0.62 * mm});
            skCircle(sketch, "E11.0.18.12", {"center": v(-8.95, -30.66) * mm, "radius": 0.62 * mm});
            skCircle(sketch, "E11.0.18.13", {"center": v(-8.95, -33.9) * mm, "radius": 0.62 * mm});
            skCircle(sketch, "E11.0.18.14", {"center": v(-8.95, -37.16) * mm, "radius": 0.62 * mm});
            skCircle(sketch, "E11.0.18.15", {"center": v(-8.95, -40.4) * mm, "radius": 0.62 * mm});
            skCircle(sketch, "E11.0.19.6", {"center": v(-5.7, -11.16) * mm, "radius": 0.62 * mm});
            skCircle(sketch, "E11.0.19.7", {"center": v(-5.7, -14.4) * mm, "radius": 0.62 * mm});
            skCircle(sketch, "E11.0.19.8", {"center": v(-5.7, -17.66) * mm, "radius": 0.62 * mm});
            skCircle(sketch, "E11.0.19.9", {"center": v(-5.7, -20.9) * mm, "radius": 0.62 * mm});
            skCircle(sketch, "E11.0.19.10", {"center": v(-5.7, -24.16) * mm, "radius": 0.62 * mm});
            skCircle(sketch, "E11.0.19.11", {"center": v(-5.7, -27.4) * mm, "radius": 0.62 * mm});
            skCircle(sketch, "E11.0.19.12", {"center": v(-5.7, -30.66) * mm, "radius": 0.62 * mm});
            skCircle(sketch, "E11.0.19.13", {"center": v(-5.7, -33.9) * mm, "radius": 0.62 * mm});
            skCircle(sketch, "E11.0.19.14", {"center": v(-5.7, -37.16) * mm, "radius": 0.62 * mm});
            skCircle(sketch, "E11.0.19.15", {"center": v(-5.7, -40.4) * mm, "radius": 0.62 * mm});
            skCircle(sketch, "E11.0.20.6", {"center": v(-2.45, -11.16) * mm, "radius": 0.62 * mm});
            skCircle(sketch, "E11.0.20.7", {"center": v(-2.45, -14.4) * mm, "radius": 0.62 * mm});
            skCircle(sketch, "E11.0.20.8", {"center": v(-2.45, -17.66) * mm, "radius": 0.62 * mm});
            skCircle(sketch, "E11.0.20.9", {"center": v(-2.45, -20.9) * mm, "radius": 0.62 * mm});
            skCircle(sketch, "E11.0.20.10", {"center": v(-2.45, -24.16) * mm, "radius": 0.62 * mm});
            skCircle(sketch, "E11.0.20.11", {"center": v(-2.45, -27.4) * mm, "radius": 0.62 * mm});
            skCircle(sketch, "E11.0.20.12", {"center": v(-2.45, -30.66) * mm, "radius": 0.62 * mm});
            skCircle(sketch, "E11.0.20.13", {"center": v(-2.45, -33.9) * mm, "radius": 0.62 * mm});
            skCircle(sketch, "E11.0.20.14", {"center": v(-2.45, -37.16) * mm, "radius": 0.62 * mm});
            skCircle(sketch, "E11.0.20.15", {"center": v(-2.45, -40.4) * mm, "radius": 0.62 * mm});
            skCircle(sketch, "E11.0.21.6", {"center": v(0.8, -11.16) * mm, "radius": 0.62 * mm});
            skCircle(sketch, "E11.0.21.7", {"center": v(0.8, -14.4) * mm, "radius": 0.62 * mm});
            skCircle(sketch, "E11.0.21.8", {"center": v(0.8, -17.66) * mm, "radius": 0.62 * mm});
            skCircle(sketch, "E11.0.21.9", {"center": v(0.8, -20.9) * mm, "radius": 0.62 * mm});
            skCircle(sketch, "E11.0.21.10", {"center": v(0.8, -24.16) * mm, "radius": 0.62 * mm});
            skCircle(sketch, "E11.0.21.11", {"center": v(0.8, -27.4) * mm, "radius": 0.62 * mm});
            skCircle(sketch, "E11.0.21.12", {"center": v(0.8, -30.66) * mm, "radius": 0.62 * mm});
            skCircle(sketch, "E11.0.21.13", {"center": v(0.8, -33.9) * mm, "radius": 0.62 * mm});
            skCircle(sketch, "E11.0.21.14", {"center": v(0.8, -37.16) * mm, "radius": 0.62 * mm});
            skCircle(sketch, "E11.0.21.15", {"center": v(0.8, -40.4) * mm, "radius": 0.62 * mm});
            skCircle(sketch, "E11.0.22.6", {"center": v(4.05, -11.16) * mm, "radius": 0.62 * mm});
            skCircle(sketch, "E11.0.22.7", {"center": v(4.05, -14.4) * mm, "radius": 0.62 * mm});
            skCircle(sketch, "E11.0.22.8", {"center": v(4.05, -17.66) * mm, "radius": 0.62 * mm});
            skCircle(sketch, "E11.0.22.9", {"center": v(4.05, -20.9) * mm, "radius": 0.62 * mm});
            skCircle(sketch, "E11.0.22.10", {"center": v(4.05, -24.16) * mm, "radius": 0.62 * mm});
            skCircle(sketch, "E11.0.22.11", {"center": v(4.05, -27.4) * mm, "radius": 0.62 * mm});
            skCircle(sketch, "E11.0.22.12", {"center": v(4.05, -30.66) * mm, "radius": 0.62 * mm});
            skCircle(sketch, "E11.0.22.13", {"center": v(4.05, -33.9) * mm, "radius": 0.62 * mm});
            skCircle(sketch, "E11.0.22.14", {"center": v(4.05, -37.16) * mm, "radius": 0.62 * mm});
            skCircle(sketch, "E11.0.22.15", {"center": v(4.05, -40.4) * mm, "radius": 0.62 * mm});
            skCircle(sketch, "E11.0.23.6", {"center": v(7.3, -11.16) * mm, "radius": 0.62 * mm});
            skCircle(sketch, "E11.0.23.7", {"center": v(7.3, -14.4) * mm, "radius": 0.62 * mm});
            skCircle(sketch, "E11.0.23.8", {"center": v(7.3, -17.66) * mm, "radius": 0.62 * mm});
            skCircle(sketch, "E11.0.23.9", {"center": v(7.3, -20.9) * mm, "radius": 0.62 * mm});
            skCircle(sketch, "E11.0.23.10", {"center": v(7.3, -24.16) * mm, "radius": 0.62 * mm});
            skCircle(sketch, "E11.0.23.11", {"center": v(7.3, -27.4) * mm, "radius": 0.62 * mm});
            skCircle(sketch, "E11.0.23.12", {"center": v(7.3, -30.66) * mm, "radius": 0.62 * mm});
            skCircle(sketch, "E11.0.23.13", {"center": v(7.3, -33.9) * mm, "radius": 0.62 * mm});
            skCircle(sketch, "E11.0.23.14", {"center": v(7.3, -37.16) * mm, "radius": 0.62 * mm});
            skCircle(sketch, "E11.0.23.15", {"center": v(7.3, -40.4) * mm, "radius": 0.62 * mm});
            skCircle(sketch, "E11.0.24.6", {"center": v(10.55, -11.16) * mm, "radius": 0.62 * mm});
            skCircle(sketch, "E11.0.24.7", {"center": v(10.55, -14.4) * mm, "radius": 0.62 * mm});
            skCircle(sketch, "E11.0.24.8", {"center": v(10.55, -17.66) * mm, "radius": 0.62 * mm});
            skCircle(sketch, "E11.0.24.9", {"center": v(10.55, -20.9) * mm, "radius": 0.62 * mm});
            skCircle(sketch, "E11.0.24.10", {"center": v(10.55, -24.16) * mm, "radius": 0.62 * mm});
            skCircle(sketch, "E11.0.24.11", {"center": v(10.55, -27.4) * mm, "radius": 0.62 * mm});
            skCircle(sketch, "E11.0.24.12", {"center": v(10.55, -30.66) * mm, "radius": 0.62 * mm});
            skCircle(sketch, "E11.0.24.13", {"center": v(10.55, -33.9) * mm, "radius": 0.62 * mm});
            skCircle(sketch, "E11.0.24.14", {"center": v(10.55, -37.16) * mm, "radius": 0.62 * mm});
            skCircle(sketch, "E11.0.24.15", {"center": v(10.55, -40.4) * mm, "radius": 0.62 * mm});
            skCircle(sketch, "E11.0.25.6", {"center": v(13.8, -11.16) * mm, "radius": 0.62 * mm});
            skCircle(sketch, "E11.0.25.7", {"center": v(13.8, -14.4) * mm, "radius": 0.62 * mm});
            skCircle(sketch, "E11.0.25.8", {"center": v(13.8, -17.66) * mm, "radius": 0.62 * mm});
            skCircle(sketch, "E11.0.25.9", {"center": v(13.8, -20.9) * mm, "radius": 0.62 * mm});
            skCircle(sketch, "E11.0.25.10", {"center": v(13.8, -24.16) * mm, "radius": 0.62 * mm});
            skCircle(sketch, "E11.0.25.11", {"center": v(13.8, -27.4) * mm, "radius": 0.62 * mm});
            skCircle(sketch, "E11.0.25.12", {"center": v(13.8, -30.66) * mm, "radius": 0.62 * mm});
            skCircle(sketch, "E11.0.25.13", {"center": v(13.8, -33.9) * mm, "radius": 0.62 * mm});
            skCircle(sketch, "E11.0.25.14", {"center": v(13.8, -37.16) * mm, "radius": 0.62 * mm});
            skCircle(sketch, "E11.0.25.15", {"center": v(13.8, -40.4) * mm, "radius": 0.62 * mm});
            skCircle(sketch, "E11.0.26.6", {"center": v(17.05, -11.16) * mm, "radius": 0.62 * mm});
            skCircle(sketch, "E11.0.26.7", {"center": v(17.05, -14.4) * mm, "radius": 0.62 * mm});
            skCircle(sketch, "E11.0.26.8", {"center": v(17.05, -17.66) * mm, "radius": 0.62 * mm});
            skCircle(sketch, "E11.0.26.9", {"center": v(17.05, -20.9) * mm, "radius": 0.62 * mm});
            skCircle(sketch, "E11.0.26.10", {"center": v(17.05, -24.16) * mm, "radius": 0.62 * mm});
            skCircle(sketch, "E11.0.26.11", {"center": v(17.05, -27.4) * mm, "radius": 0.62 * mm});
            skCircle(sketch, "E11.0.26.12", {"center": v(17.05, -30.66) * mm, "radius": 0.62 * mm});
            skCircle(sketch, "E11.0.26.13", {"center": v(17.05, -33.9) * mm, "radius": 0.62 * mm});
            skCircle(sketch, "E11.0.26.14", {"center": v(17.05, -37.16) * mm, "radius": 0.62 * mm});
            skCircle(sketch, "E11.0.26.15", {"center": v(17.05, -40.4) * mm, "radius": 0.62 * mm});
            skCircle(sketch, "E11.0.27.6", {"center": v(20.3, -11.16) * mm, "radius": 0.62 * mm});
            skCircle(sketch, "E11.0.27.7", {"center": v(20.3, -14.4) * mm, "radius": 0.62 * mm});
            skCircle(sketch, "E11.0.27.8", {"center": v(20.3, -17.66) * mm, "radius": 0.62 * mm});
            skCircle(sketch, "E11.0.27.9", {"center": v(20.3, -20.9) * mm, "radius": 0.62 * mm});
            skCircle(sketch, "E11.0.27.10", {"center": v(20.3, -24.16) * mm, "radius": 0.62 * mm});
            skCircle(sketch, "E11.0.27.11", {"center": v(20.3, -27.4) * mm, "radius": 0.62 * mm});
            skCircle(sketch, "E11.0.27.12", {"center": v(20.3, -30.66) * mm, "radius": 0.62 * mm});
            skCircle(sketch, "E11.0.27.13", {"center": v(20.3, -33.9) * mm, "radius": 0.62 * mm});
            skCircle(sketch, "E11.0.27.14", {"center": v(20.3, -37.16) * mm, "radius": 0.62 * mm});
            skCircle(sketch, "E11.0.27.15", {"center": v(20.3, -40.4) * mm, "radius": 0.62 * mm});
            skCircle(sketch, "E11.0.28.6", {"center": v(23.55, -11.16) * mm, "radius": 0.62 * mm});
            skCircle(sketch, "E11.0.28.7", {"center": v(23.55, -14.4) * mm, "radius": 0.62 * mm});
            skCircle(sketch, "E11.0.28.8", {"center": v(23.55, -17.66) * mm, "radius": 0.62 * mm});
            skCircle(sketch, "E11.0.28.9", {"center": v(23.55, -20.9) * mm, "radius": 0.62 * mm});
            skCircle(sketch, "E11.0.28.10", {"center": v(23.55, -24.16) * mm, "radius": 0.62 * mm});
            skCircle(sketch, "E11.0.28.11", {"center": v(23.55, -27.4) * mm, "radius": 0.62 * mm});
            skCircle(sketch, "E11.0.28.12", {"center": v(23.55, -30.66) * mm, "radius": 0.62 * mm});
            skCircle(sketch, "E11.0.28.13", {"center": v(23.55, -33.9) * mm, "radius": 0.62 * mm});
            skCircle(sketch, "E11.0.28.14", {"center": v(23.55, -37.16) * mm, "radius": 0.62 * mm});
            skCircle(sketch, "E11.0.28.15", {"center": v(23.55, -40.4) * mm, "radius": 0.62 * mm});
            skCircle(sketch, "E11.0.29.6", {"center": v(26.8, -11.16) * mm, "radius": 0.62 * mm});
            skCircle(sketch, "E11.0.29.7", {"center": v(26.8, -14.4) * mm, "radius": 0.62 * mm});
            skCircle(sketch, "E11.0.29.8", {"center": v(26.8, -17.66) * mm, "radius": 0.62 * mm});
            skCircle(sketch, "E11.0.29.9", {"center": v(26.8, -20.9) * mm, "radius": 0.62 * mm});
            skCircle(sketch, "E11.0.29.10", {"center": v(26.8, -24.16) * mm, "radius": 0.62 * mm});
            skCircle(sketch, "E11.0.29.11", {"center": v(26.8, -27.4) * mm, "radius": 0.62 * mm});
            skCircle(sketch, "E11.0.29.12", {"center": v(26.8, -30.66) * mm, "radius": 0.62 * mm});
            skCircle(sketch, "E11.0.29.13", {"center": v(26.8, -33.9) * mm, "radius": 0.62 * mm});
            skCircle(sketch, "E11.0.29.14", {"center": v(26.8, -37.16) * mm, "radius": 0.62 * mm});
            skCircle(sketch, "E11.0.29.15", {"center": v(26.8, -40.4) * mm, "radius": 0.62 * mm});
            skCircle(sketch, "E11.0.30.6", {"center": v(30.05, -11.16) * mm, "radius": 0.62 * mm});
            skCircle(sketch, "E11.0.30.7", {"center": v(30.05, -14.4) * mm, "radius": 0.62 * mm});
            skCircle(sketch, "E11.0.30.8", {"center": v(30.05, -17.66) * mm, "radius": 0.62 * mm});
            skCircle(sketch, "E11.0.30.9", {"center": v(30.05, -20.9) * mm, "radius": 0.62 * mm});
            skCircle(sketch, "E11.0.30.10", {"center": v(30.05, -24.16) * mm, "radius": 0.62 * mm});
            skCircle(sketch, "E11.0.30.11", {"center": v(30.05, -27.4) * mm, "radius": 0.62 * mm});
            skCircle(sketch, "E11.0.30.12", {"center": v(30.05, -30.66) * mm, "radius": 0.62 * mm});
            skCircle(sketch, "E11.0.30.13", {"center": v(30.05, -33.9) * mm, "radius": 0.62 * mm});
            skCircle(sketch, "E11.0.30.14", {"center": v(30.05, -37.16) * mm, "radius": 0.62 * mm});
            skCircle(sketch, "E11.0.30.15", {"center": v(30.05, -40.4) * mm, "radius": 0.62 * mm});
            skCircle(sketch, "E11.0.31.6", {"center": v(33.3, -11.16) * mm, "radius": 0.62 * mm});
            skCircle(sketch, "E11.0.31.7", {"center": v(33.3, -14.4) * mm, "radius": 0.62 * mm});
            skCircle(sketch, "E11.0.31.8", {"center": v(33.3, -17.66) * mm, "radius": 0.62 * mm});
            skCircle(sketch, "E11.0.31.9", {"center": v(33.3, -20.9) * mm, "radius": 0.62 * mm});
            skCircle(sketch, "E11.0.31.10", {"center": v(33.3, -24.16) * mm, "radius": 0.62 * mm});
            skCircle(sketch, "E11.0.31.11", {"center": v(33.3, -27.4) * mm, "radius": 0.62 * mm});
            skCircle(sketch, "E11.0.31.12", {"center": v(33.3, -30.66) * mm, "radius": 0.62 * mm});
            skCircle(sketch, "E11.0.31.13", {"center": v(33.3, -33.9) * mm, "radius": 0.62 * mm});
            skCircle(sketch, "E11.0.31.14", {"center": v(33.3, -37.16) * mm, "radius": 0.62 * mm});
            skCircle(sketch, "E11.0.31.15", {"center": v(33.3, -40.4) * mm, "radius": 0.62 * mm});
            skCircle(sketch, "E11.0.32.6", {"center": v(36.55, -11.16) * mm, "radius": 0.62 * mm});
            skCircle(sketch, "E11.0.32.7", {"center": v(36.55, -14.4) * mm, "radius": 0.62 * mm});
            skCircle(sketch, "E11.0.32.8", {"center": v(36.55, -17.66) * mm, "radius": 0.62 * mm});
            skCircle(sketch, "E11.0.32.9", {"center": v(36.55, -20.9) * mm, "radius": 0.62 * mm});
            skCircle(sketch, "E11.0.32.10", {"center": v(36.55, -24.16) * mm, "radius": 0.62 * mm});
            skCircle(sketch, "E11.0.32.11", {"center": v(36.55, -27.4) * mm, "radius": 0.62 * mm});
            skCircle(sketch, "E11.0.32.12", {"center": v(36.55, -30.66) * mm, "radius": 0.62 * mm});
            skCircle(sketch, "E11.0.32.13", {"center": v(36.55, -33.9) * mm, "radius": 0.62 * mm});
            skCircle(sketch, "E11.0.32.14", {"center": v(36.55, -37.16) * mm, "radius": 0.62 * mm});
            skCircle(sketch, "E11.0.32.15", {"center": v(36.55, -40.4) * mm, "radius": 0.62 * mm});
            skCircle(sketch, "E11.0.33.6", {"center": v(39.8, -11.16) * mm, "radius": 0.62 * mm});
            skCircle(sketch, "E11.0.33.7", {"center": v(39.8, -14.4) * mm, "radius": 0.62 * mm});
            skCircle(sketch, "E11.0.33.8", {"center": v(39.8, -17.66) * mm, "radius": 0.62 * mm});
            skCircle(sketch, "E11.0.33.9", {"center": v(39.8, -20.9) * mm, "radius": 0.62 * mm});
            skCircle(sketch, "E11.0.33.10", {"center": v(39.8, -24.16) * mm, "radius": 0.62 * mm});
            skCircle(sketch, "E11.0.33.11", {"center": v(39.8, -27.4) * mm, "radius": 0.62 * mm});
            skCircle(sketch, "E11.0.33.12", {"center": v(39.8, -30.66) * mm, "radius": 0.62 * mm});
            skCircle(sketch, "E11.0.33.13", {"center": v(39.8, -33.9) * mm, "radius": 0.62 * mm});
            skCircle(sketch, "E11.0.33.14", {"center": v(39.8, -37.16) * mm, "radius": 0.62 * mm});
            skCircle(sketch, "E11.0.33.15", {"center": v(39.8, -40.4) * mm, "radius": 0.62 * mm});
            skCircle(sketch, "E11.0.34.6", {"center": v(43.05, -11.16) * mm, "radius": 0.62 * mm});
            skCircle(sketch, "E11.0.34.7", {"center": v(43.05, -14.4) * mm, "radius": 0.62 * mm});
            skCircle(sketch, "E11.0.34.8", {"center": v(43.05, -17.66) * mm, "radius": 0.62 * mm});
            skCircle(sketch, "E11.0.34.9", {"center": v(43.05, -20.9) * mm, "radius": 0.62 * mm});
            skCircle(sketch, "E11.0.34.10", {"center": v(43.05, -24.16) * mm, "radius": 0.62 * mm});
            skCircle(sketch, "E11.0.34.11", {"center": v(43.05, -27.4) * mm, "radius": 0.62 * mm});
            skCircle(sketch, "E11.0.34.12", {"center": v(43.05, -30.66) * mm, "radius": 0.62 * mm});
            skCircle(sketch, "E11.0.34.13", {"center": v(43.05, -33.9) * mm, "radius": 0.62 * mm});
            skCircle(sketch, "E11.0.34.14", {"center": v(43.05, -37.16) * mm, "radius": 0.62 * mm});
            skCircle(sketch, "E11.0.34.15", {"center": v(43.05, -40.4) * mm, "radius": 0.62 * mm});
            skCircle(sketch, "E11.0.35.6", {"center": v(46.3, -11.16) * mm, "radius": 0.62 * mm});
            skCircle(sketch, "E11.0.35.7", {"center": v(46.3, -14.4) * mm, "radius": 0.62 * mm});
            skCircle(sketch, "E11.0.35.8", {"center": v(46.3, -17.66) * mm, "radius": 0.62 * mm});
            skCircle(sketch, "E11.0.35.9", {"center": v(46.3, -20.9) * mm, "radius": 0.62 * mm});
            skCircle(sketch, "E11.0.35.10", {"center": v(46.3, -24.16) * mm, "radius": 0.62 * mm});
            skCircle(sketch, "E11.0.35.11", {"center": v(46.3, -27.4) * mm, "radius": 0.62 * mm});
            skCircle(sketch, "E11.0.35.12", {"center": v(46.3, -30.66) * mm, "radius": 0.62 * mm});
            skCircle(sketch, "E11.0.35.13", {"center": v(46.3, -33.9) * mm, "radius": 0.62 * mm});
            skCircle(sketch, "E11.0.35.14", {"center": v(46.3, -37.16) * mm, "radius": 0.62 * mm});
            skCircle(sketch, "E11.0.35.15", {"center": v(46.3, -40.4) * mm, "radius": 0.62 * mm});
            skCircle(sketch, "E11.0.36.6", {"center": v(49.55, -11.16) * mm, "radius": 0.62 * mm});
            skCircle(sketch, "E11.0.36.7", {"center": v(49.55, -14.4) * mm, "radius": 0.62 * mm});
            skCircle(sketch, "E11.0.36.8", {"center": v(49.55, -17.66) * mm, "radius": 0.62 * mm});
            skCircle(sketch, "E11.0.36.9", {"center": v(49.55, -20.9) * mm, "radius": 0.62 * mm});
            skCircle(sketch, "E11.0.36.10", {"center": v(49.55, -24.16) * mm, "radius": 0.62 * mm});
            skCircle(sketch, "E11.0.36.11", {"center": v(49.55, -27.4) * mm, "radius": 0.62 * mm});
            skCircle(sketch, "E11.0.36.12", {"center": v(49.55, -30.66) * mm, "radius": 0.62 * mm});
            skCircle(sketch, "E11.0.36.13", {"center": v(49.55, -33.9) * mm, "radius": 0.62 * mm});
            skCircle(sketch, "E11.0.36.14", {"center": v(49.55, -37.16) * mm, "radius": 0.62 * mm});
            skCircle(sketch, "E11.0.36.15", {"center": v(49.55, -40.4) * mm, "radius": 0.62 * mm});
            skCircle(sketch, "E11.0.37.6", {"center": v(52.8, -11.16) * mm, "radius": 0.62 * mm});
            skCircle(sketch, "E11.0.37.7", {"center": v(52.8, -14.4) * mm, "radius": 0.62 * mm});
            skCircle(sketch, "E11.0.37.8", {"center": v(52.8, -17.66) * mm, "radius": 0.62 * mm});
            skCircle(sketch, "E11.0.37.9", {"center": v(52.8, -20.9) * mm, "radius": 0.62 * mm});
            skCircle(sketch, "E11.0.37.10", {"center": v(52.8, -24.16) * mm, "radius": 0.62 * mm});
            skCircle(sketch, "E11.0.37.11", {"center": v(52.8, -27.4) * mm, "radius": 0.62 * mm});
            skCircle(sketch, "E11.0.37.12", {"center": v(52.8, -30.66) * mm, "radius": 0.62 * mm});
            skCircle(sketch, "E11.0.37.13", {"center": v(52.8, -33.9) * mm, "radius": 0.62 * mm});
            skCircle(sketch, "E11.0.37.14", {"center": v(52.8, -37.16) * mm, "radius": 0.62 * mm});
            skCircle(sketch, "E11.0.37.15", {"center": v(52.8, -40.4) * mm, "radius": 0.62 * mm});
            skCircle(sketch, "E11.0.38.6", {"center": v(56.05, -11.16) * mm, "radius": 0.62 * mm});
            skCircle(sketch, "E11.0.38.7", {"center": v(56.05, -14.4) * mm, "radius": 0.62 * mm});
            skCircle(sketch, "E11.0.38.8", {"center": v(56.05, -17.66) * mm, "radius": 0.62 * mm});
            skCircle(sketch, "E11.0.38.9", {"center": v(56.05, -20.9) * mm, "radius": 0.62 * mm});
            skCircle(sketch, "E11.0.38.10", {"center": v(56.05, -24.16) * mm, "radius": 0.62 * mm});
            skCircle(sketch, "E11.0.38.11", {"center": v(56.05, -27.4) * mm, "radius": 0.62 * mm});
            skCircle(sketch, "E11.0.38.12", {"center": v(56.05, -30.66) * mm, "radius": 0.62 * mm});
            skCircle(sketch, "E11.0.38.13", {"center": v(56.05, -33.9) * mm, "radius": 0.62 * mm});
            skCircle(sketch, "E11.0.38.14", {"center": v(56.05, -37.16) * mm, "radius": 0.62 * mm});
            skCircle(sketch, "E11.0.38.15", {"center": v(56.05, -40.4) * mm, "radius": 0.62 * mm});
            skCircle(sketch, "E11.0.39.6", {"center": v(59.3, -11.16) * mm, "radius": 0.62 * mm});
            skCircle(sketch, "E11.0.39.7", {"center": v(59.3, -14.4) * mm, "radius": 0.62 * mm});
            skCircle(sketch, "E11.0.39.8", {"center": v(59.3, -17.66) * mm, "radius": 0.62 * mm});
            skCircle(sketch, "E11.0.39.9", {"center": v(59.3, -20.9) * mm, "radius": 0.62 * mm});
            skCircle(sketch, "E11.0.39.10", {"center": v(59.3, -24.16) * mm, "radius": 0.62 * mm});
            skCircle(sketch, "E11.0.39.11", {"center": v(59.3, -27.4) * mm, "radius": 0.62 * mm});
            skCircle(sketch, "E11.0.39.12", {"center": v(59.3, -30.66) * mm, "radius": 0.62 * mm});
            skCircle(sketch, "E11.0.39.13", {"center": v(59.3, -33.9) * mm, "radius": 0.62 * mm});
            skCircle(sketch, "E11.0.39.14", {"center": v(59.3, -37.16) * mm, "radius": 0.62 * mm});
            skCircle(sketch, "E11.0.39.15", {"center": v(59.3, -40.4) * mm, "radius": 0.62 * mm});
            skCircle(sketch, "E11.0.40.6", {"center": v(62.55, -11.16) * mm, "radius": 0.62 * mm});
            skCircle(sketch, "E11.0.40.7", {"center": v(62.55, -14.4) * mm, "radius": 0.62 * mm});
            skCircle(sketch, "E11.0.40.8", {"center": v(62.55, -17.66) * mm, "radius": 0.62 * mm});
            skCircle(sketch, "E11.0.40.9", {"center": v(62.55, -20.9) * mm, "radius": 0.62 * mm});
            skCircle(sketch, "E11.0.40.10", {"center": v(62.55, -24.16) * mm, "radius": 0.62 * mm});
            skCircle(sketch, "E11.0.40.11", {"center": v(62.55, -27.4) * mm, "radius": 0.62 * mm});
            skCircle(sketch, "E11.0.40.12", {"center": v(62.55, -30.66) * mm, "radius": 0.62 * mm});
            skCircle(sketch, "E11.0.40.13", {"center": v(62.55, -33.9) * mm, "radius": 0.62 * mm});
            skCircle(sketch, "E11.0.40.14", {"center": v(62.55, -37.16) * mm, "radius": 0.62 * mm});
            skCircle(sketch, "E11.0.40.15", {"center": v(62.55, -40.4) * mm, "radius": 0.62 * mm});
            skCircle(sketch, "E11.0.41.6", {"center": v(65.8, -11.16) * mm, "radius": 0.62 * mm});
            skCircle(sketch, "E11.0.41.7", {"center": v(65.8, -14.4) * mm, "radius": 0.62 * mm});
            skCircle(sketch, "E11.0.41.8", {"center": v(65.8, -17.66) * mm, "radius": 0.62 * mm});
            skCircle(sketch, "E11.0.41.9", {"center": v(65.8, -20.9) * mm, "radius": 0.62 * mm});
            skCircle(sketch, "E11.0.41.10", {"center": v(65.8, -24.16) * mm, "radius": 0.62 * mm});
            skCircle(sketch, "E11.0.41.11", {"center": v(65.8, -27.4) * mm, "radius": 0.62 * mm});
            skCircle(sketch, "E11.0.41.12", {"center": v(65.8, -30.66) * mm, "radius": 0.62 * mm});
            skCircle(sketch, "E11.0.41.13", {"center": v(65.8, -33.9) * mm, "radius": 0.62 * mm});
            skCircle(sketch, "E11.0.41.14", {"center": v(65.8, -37.16) * mm, "radius": 0.62 * mm});
            skCircle(sketch, "E11.0.41.15", {"center": v(65.8, -40.4) * mm, "radius": 0.62 * mm});
            skCircle(sketch, "E11.0.42.6", {"center": v(69.05, -11.16) * mm, "radius": 0.62 * mm});
            skCircle(sketch, "E11.0.42.7", {"center": v(69.05, -14.4) * mm, "radius": 0.62 * mm});
            skCircle(sketch, "E11.0.42.8", {"center": v(69.05, -17.66) * mm, "radius": 0.62 * mm});
            skCircle(sketch, "E11.0.42.9", {"center": v(69.05, -20.9) * mm, "radius": 0.62 * mm});
            skCircle(sketch, "E11.0.42.10", {"center": v(69.05, -24.16) * mm, "radius": 0.62 * mm});
            skCircle(sketch, "E11.0.42.11", {"center": v(69.05, -27.4) * mm, "radius": 0.62 * mm});
            skCircle(sketch, "E11.0.42.12", {"center": v(69.05, -30.66) * mm, "radius": 0.62 * mm});
            skCircle(sketch, "E11.0.42.13", {"center": v(69.05, -33.9) * mm, "radius": 0.62 * mm});
            skCircle(sketch, "E11.0.42.14", {"center": v(69.05, -37.16) * mm, "radius": 0.62 * mm});
            skCircle(sketch, "E11.0.42.15", {"center": v(69.05, -40.4) * mm, "radius": 0.62 * mm});
            skCircle(sketch, "E11.0.43.6", {"center": v(72.3, -11.16) * mm, "radius": 0.62 * mm});
            skCircle(sketch, "E11.0.43.7", {"center": v(72.3, -14.4) * mm, "radius": 0.62 * mm});
            skCircle(sketch, "E11.0.43.8", {"center": v(72.3, -17.66) * mm, "radius": 0.62 * mm});
            skCircle(sketch, "E11.0.43.9", {"center": v(72.3, -20.9) * mm, "radius": 0.62 * mm});
            skCircle(sketch, "E11.0.43.10", {"center": v(72.3, -24.16) * mm, "radius": 0.62 * mm});
            skCircle(sketch, "E11.0.43.11", {"center": v(72.3, -27.4) * mm, "radius": 0.62 * mm});
            skCircle(sketch, "E11.0.43.12", {"center": v(72.3, -30.66) * mm, "radius": 0.62 * mm});
            skCircle(sketch, "E11.0.43.13", {"center": v(72.3, -33.9) * mm, "radius": 0.62 * mm});
            skCircle(sketch, "E11.0.43.14", {"center": v(72.3, -37.16) * mm, "radius": 0.62 * mm});
            skCircle(sketch, "E11.0.43.15", {"center": v(72.3, -40.4) * mm, "radius": 0.62 * mm});
            skCircle(sketch, "E11.0.44.6", {"center": v(75.55, -11.16) * mm, "radius": 0.62 * mm});
            skCircle(sketch, "E11.0.44.7", {"center": v(75.55, -14.4) * mm, "radius": 0.62 * mm});
            skCircle(sketch, "E11.0.44.8", {"center": v(75.55, -17.66) * mm, "radius": 0.62 * mm});
            skCircle(sketch, "E11.0.44.9", {"center": v(75.55, -20.9) * mm, "radius": 0.62 * mm});
            skCircle(sketch, "E11.0.44.10", {"center": v(75.55, -24.16) * mm, "radius": 0.62 * mm});
            skCircle(sketch, "E11.0.44.11", {"center": v(75.55, -27.4) * mm, "radius": 0.62 * mm});
            skCircle(sketch, "E11.0.44.12", {"center": v(75.55, -30.66) * mm, "radius": 0.62 * mm});
            skCircle(sketch, "E11.0.44.13", {"center": v(75.55, -33.9) * mm, "radius": 0.62 * mm});
            skCircle(sketch, "E11.0.44.14", {"center": v(75.55, -37.16) * mm, "radius": 0.62 * mm});
            skCircle(sketch, "E11.0.44.15", {"center": v(75.55, -40.4) * mm, "radius": 0.62 * mm});
            skCircle(sketch, "E12.0.0.15", {"center": v(-69.07, -38.78) * mm, "radius": 0.62 * mm});
            skCircle(sketch, "E12.0.1.15", {"center": v(-65.82, -38.78) * mm, "radius": 0.62 * mm});
            skCircle(sketch, "E12.0.2.15", {"center": v(-62.57, -38.78) * mm, "radius": 0.62 * mm});
            skCircle(sketch, "E12.0.3.15", {"center": v(-59.32, -38.78) * mm, "radius": 0.62 * mm});
            skCircle(sketch, "E12.0.4.15", {"center": v(-56.07, -38.78) * mm, "radius": 0.62 * mm});
            skCircle(sketch, "E12.0.5.15", {"center": v(-52.82, -38.78) * mm, "radius": 0.62 * mm});
            skCircle(sketch, "E12.0.6.15", {"center": v(-49.57, -38.78) * mm, "radius": 0.62 * mm});
            skCircle(sketch, "E12.0.7.15", {"center": v(-46.32, -38.78) * mm, "radius": 0.62 * mm});
            skCircle(sketch, "E12.0.8.15", {"center": v(-43.07, -38.78) * mm, "radius": 0.62 * mm});
            skCircle(sketch, "E12.0.9.15", {"center": v(-39.82, -38.78) * mm, "radius": 0.62 * mm});
            skCircle(sketch, "E12.0.10.15", {"center": v(-36.57, -38.78) * mm, "radius": 0.62 * mm});
            skCircle(sketch, "E12.0.11.15", {"center": v(-33.32, -38.78) * mm, "radius": 0.62 * mm});
            skCircle(sketch, "E12.0.12.15", {"center": v(-30.07, -38.78) * mm, "radius": 0.62 * mm});
            skCircle(sketch, "E12.0.13.15", {"center": v(-26.82, -38.78) * mm, "radius": 0.62 * mm});
            skCircle(sketch, "E12.0.14.15", {"center": v(-23.57, -38.78) * mm, "radius": 0.62 * mm});
            skCircle(sketch, "E12.0.15.15", {"center": v(-20.32, -38.78) * mm, "radius": 0.62 * mm});
            skCircle(sketch, "E12.0.16.15", {"center": v(-17.07, -38.78) * mm, "radius": 0.62 * mm});
            skCircle(sketch, "E12.0.17.15", {"center": v(-13.82, -38.78) * mm, "radius": 0.62 * mm});
            skCircle(sketch, "E12.0.18.15", {"center": v(-10.57, -38.78) * mm, "radius": 0.62 * mm});
            skCircle(sketch, "E12.0.19.15", {"center": v(-7.32, -38.78) * mm, "radius": 0.62 * mm});
            skCircle(sketch, "E12.0.20.15", {"center": v(-4.07, -38.78) * mm, "radius": 0.62 * mm});
            skCircle(sketch, "E12.0.21.15", {"center": v(-0.82, -38.78) * mm, "radius": 0.62 * mm});
            skCircle(sketch, "E12.0.22.15", {"center": v(2.43, -38.78) * mm, "radius": 0.62 * mm});
            skCircle(sketch, "E12.0.23.15", {"center": v(5.68, -38.78) * mm, "radius": 0.62 * mm});
            skCircle(sketch, "E12.0.24.15", {"center": v(8.93, -38.78) * mm, "radius": 0.62 * mm});
            skCircle(sketch, "E12.0.25.15", {"center": v(12.18, -38.78) * mm, "radius": 0.62 * mm});
            skCircle(sketch, "E12.0.26.15", {"center": v(15.43, -38.78) * mm, "radius": 0.62 * mm});
            skCircle(sketch, "E12.0.27.15", {"center": v(18.68, -38.78) * mm, "radius": 0.62 * mm});
            skCircle(sketch, "E12.0.28.15", {"center": v(21.93, -38.78) * mm, "radius": 0.62 * mm});
            skCircle(sketch, "E12.0.29.15", {"center": v(25.18, -38.78) * mm, "radius": 0.62 * mm});
            skCircle(sketch, "E12.0.30.15", {"center": v(28.43, -38.78) * mm, "radius": 0.62 * mm});
            skCircle(sketch, "E12.0.31.15", {"center": v(31.68, -38.78) * mm, "radius": 0.62 * mm});
            skCircle(sketch, "E12.0.32.15", {"center": v(34.93, -38.78) * mm, "radius": 0.62 * mm});
            skCircle(sketch, "E12.0.33.15", {"center": v(38.18, -38.78) * mm, "radius": 0.62 * mm});
            skCircle(sketch, "E12.0.34.15", {"center": v(41.43, -38.78) * mm, "radius": 0.62 * mm});
            skCircle(sketch, "E12.0.35.15", {"center": v(44.68, -38.78) * mm, "radius": 0.62 * mm});
            skCircle(sketch, "E12.0.36.15", {"center": v(47.93, -38.78) * mm, "radius": 0.62 * mm});
            skCircle(sketch, "E12.0.37.15", {"center": v(51.18, -38.78) * mm, "radius": 0.62 * mm});
            skCircle(sketch, "E12.0.38.15", {"center": v(54.43, -38.78) * mm, "radius": 0.62 * mm});
            skCircle(sketch, "E12.0.39.15", {"center": v(57.68, -38.78) * mm, "radius": 0.62 * mm});
            skCircle(sketch, "E12.0.40.15", {"center": v(60.93, -38.78) * mm, "radius": 0.62 * mm});
            skCircle(sketch, "E12.0.41.15", {"center": v(64.18, -38.78) * mm, "radius": 0.62 * mm});
            skCircle(sketch, "E12.0.42.15", {"center": v(67.43, -38.78) * mm, "radius": 0.62 * mm});
            skCircle(sketch, "E12.0.43.15", {"center": v(70.68, -38.78) * mm, "radius": 0.62 * mm});
            skCircle(sketch, "E12.0.44.15", {"center": v(73.93, -38.78) * mm, "radius": 0.62 * mm});
            skSolve(sketch);
        }
        {
            var Q0;
            Q0=qSketchRegion(id+"F0",true);
            extrude(context, id + "F1", {"entities" : qUnion([Q0]), "depth" : 0.5 * mm, "offsetDistance" : 25.4 * mm});
        }
    });
